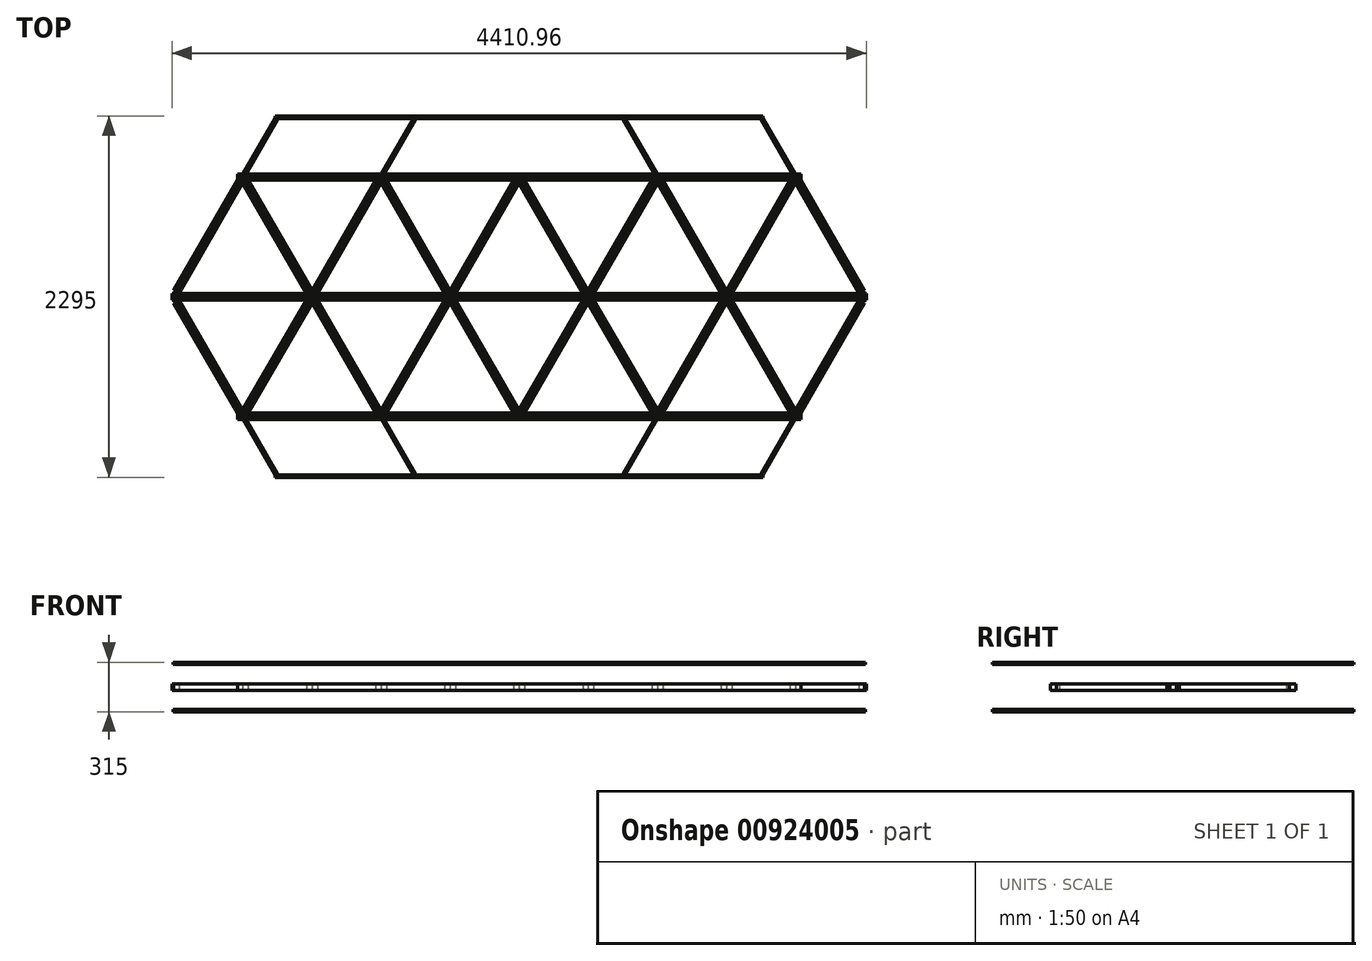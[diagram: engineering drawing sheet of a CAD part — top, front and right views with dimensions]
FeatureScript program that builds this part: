
annotation { "Feature Type Name" : "Feature", "Feature Type Description" : "" }
export const myFeature = defineFeature(function(context is Context, id is Id, definition is map)
    precondition{}
    {
        {
            var Q0;
            Q0=qCreatedBy(makeId("Top.planeOp"),FACE);
            var sketch = newSketch(context, id + "F0", { "sketchPlane" : qUnion([Q0])});
            skLineSegment(sketch, "E0", {"start": v(-2194.22, 0) * mm, "end": v(2196.22, 0) * mm, "construction": true});
            skLineSegment(sketch, "E1", {"start": v(0, 0.48) * mm, "end": v(0, -0.7) * mm, "construction": true});
            skLineSegment(sketch, "E2", {"start": v(0, 760) * mm, "end": v(438.79, 0) * mm, "construction": true});
            skLineSegment(sketch, "E3", {"start": v(438.79, 0) * mm, "end": v(877.57, 760) * mm, "construction": true});
            skLineSegment(sketch, "E4", {"start": v(0, 760) * mm, "end": v(877.57, 760) * mm, "construction": true});
            skLineSegment(sketch, "E5", {"start": v(877.57, 760) * mm, "end": v(877.57, 744.9) * mm, "construction": true});
            skLineSegment(sketch, "E6.MirrorCS", {"start": v(1316.36, 0) * mm, "end": v(877.57, 760) * mm, "construction": true});
            skLineSegment(sketch, "E7.MirrorCS", {"start": v(1755.14, 760) * mm, "end": v(1316.36, 0) * mm, "construction": true});
            skLineSegment(sketch, "E8.MirrorCS", {"start": v(1755.14, 760) * mm, "end": v(877.57, 760) * mm, "construction": true});
            skLineSegment(sketch, "E9", {"start": v(1755.14, 760) * mm, "end": v(1755.14, 750.7) * mm, "construction": true});
            skLineSegment(sketch, "E10.MirrorCS", {"start": v(1755.14, 760) * mm, "end": v(2193.93, 0) * mm, "construction": true});
            skLineSegment(sketch, "E11.MirrorCS", {"start": v(0, -760) * mm, "end": v(438.79, 0) * mm, "construction": true});
            skLineSegment(sketch, "E12.MirrorCS", {"start": v(438.79, 0) * mm, "end": v(877.57, -760) * mm, "construction": true});
            skLineSegment(sketch, "E13.MirrorCS", {"start": v(1316.36, 0) * mm, "end": v(877.57, -760) * mm, "construction": true});
            skLineSegment(sketch, "E14.MirrorCS", {"start": v(1755.14, -760) * mm, "end": v(1316.36, 0) * mm, "construction": true});
            skLineSegment(sketch, "E15.MirrorCS", {"start": v(1755.14, -760) * mm, "end": v(2193.93, 0) * mm, "construction": true});
            skLineSegment(sketch, "E16.MirrorCS", {"start": v(1755.14, -760) * mm, "end": v(877.57, -760) * mm, "construction": true});
            skLineSegment(sketch, "E17.MirrorCS", {"start": v(0, -760) * mm, "end": v(877.57, -760) * mm, "construction": true});
            skLineSegment(sketch, "E18.MirrorCS", {"start": v(-438.79, 0) * mm, "end": v(-877.57, -760) * mm, "construction": true});
            skLineSegment(sketch, "E19.MirrorCS", {"start": v(0, 760) * mm, "end": v(-438.79, 0) * mm, "construction": true});
            skLineSegment(sketch, "E20.MirrorCS", {"start": v(-438.79, 0) * mm, "end": v(-877.57, 760) * mm, "construction": true});
            skLineSegment(sketch, "E21.MirrorCS", {"start": v(0, 760) * mm, "end": v(-877.57, 760) * mm, "construction": true});
            skLineSegment(sketch, "E22.MirrorCS", {"start": v(-877.57, 760) * mm, "end": v(-877.57, 744.9) * mm, "construction": true});
            skLineSegment(sketch, "E23.MirrorCS", {"start": v(0, -760) * mm, "end": v(-438.79, 0) * mm, "construction": true});
            skLineSegment(sketch, "E24.MirrorCS", {"start": v(-1755.14, 760) * mm, "end": v(-1755.14, 750.7) * mm, "construction": true});
            skLineSegment(sketch, "E25.MirrorCS", {"start": v(-1316.36, 0) * mm, "end": v(-877.57, 760) * mm, "construction": true});
            skLineSegment(sketch, "E26.MirrorCS", {"start": v(-1755.14, 760) * mm, "end": v(-877.57, 760) * mm, "construction": true});
            skLineSegment(sketch, "E27.MirrorCS", {"start": v(-1755.14, -760) * mm, "end": v(-877.57, -760) * mm, "construction": true});
            skLineSegment(sketch, "E28.MirrorCS", {"start": v(-1755.14, 760) * mm, "end": v(-1316.36, 0) * mm, "construction": true});
            skLineSegment(sketch, "E29.MirrorCS", {"start": v(-1755.14, -760) * mm, "end": v(-2193.93, 0) * mm, "construction": true});
            skLineSegment(sketch, "E30.MirrorCS", {"start": v(-1316.36, 0) * mm, "end": v(-877.57, -760) * mm, "construction": true});
            skLineSegment(sketch, "E31.MirrorCS", {"start": v(-1755.14, -760) * mm, "end": v(-1316.36, 0) * mm, "construction": true});
            skLineSegment(sketch, "E32.MirrorCS", {"start": v(-1755.14, 760) * mm, "end": v(-2193.93, 0) * mm, "construction": true});
            skLineSegment(sketch, "E33.MirrorCS", {"start": v(0, -760) * mm, "end": v(-877.57, -760) * mm, "construction": true});
            skCircle(sketch, "E34", {"center": v(438.79, 760) * mm, "radius": 380 * mm, "construction": true});
            skLineSegment(sketch, "E35", {"start": v(438.79, 0) * mm, "end": v(1316.36, 0) * mm, "construction": true});
            skCircle(sketch, "E36", {"center": v(877.57, 0) * mm, "radius": 380 * mm, "construction": true});
            skLineSegment(sketch, "E37", {"start": v(1316.36, 0) * mm, "end": v(1316.36, -2.45) * mm, "construction": true});
            skCircle(sketch, "E38.MirrorC", {"center": v(1755.14, 0) * mm, "radius": 380 * mm, "construction": true});
            skCircle(sketch, "E39.MirrorC", {"center": v(1316.36, 760) * mm, "radius": 380 * mm, "construction": true});
            skCircle(sketch, "E40.MirrorC", {"center": v(1316.36, -760) * mm, "radius": 380 * mm, "construction": true});
            skCircle(sketch, "E41.MirrorC", {"center": v(438.79, -760) * mm, "radius": 380 * mm, "construction": true});
            skCircle(sketch, "E42.MirrorC", {"center": v(-438.79, 760) * mm, "radius": 380 * mm, "construction": true});
            skCircle(sketch, "E43.MirrorC", {"center": v(-1316.36, 760) * mm, "radius": 380 * mm, "construction": true});
            skCircle(sketch, "E44.MirrorC", {"center": v(-877.57, 0) * mm, "radius": 380 * mm, "construction": true});
            skCircle(sketch, "E45.MirrorC", {"center": v(-1755.14, 0) * mm, "radius": 380 * mm, "construction": true});
            skCircle(sketch, "E46.MirrorC", {"center": v(-1316.36, -760) * mm, "radius": 380 * mm, "construction": true});
            skCircle(sketch, "E47.MirrorC", {"center": v(-438.79, -760) * mm, "radius": 380 * mm, "construction": true});
            skLineSegment(sketch, "E48", {"start": v(0, 1140) * mm, "end": v(1535.75, 1140) * mm, "construction": true});
            skLineSegment(sketch, "E49", {"start": v(1535.75, 1140) * mm, "end": v(1755.14, 760) * mm, "construction": true});
            skLineSegment(sketch, "E50.MirrorCS", {"start": v(0, -1140) * mm, "end": v(1535.75, -1140) * mm, "construction": true});
            skLineSegment(sketch, "E51.MirrorCS", {"start": v(1535.75, -1140) * mm, "end": v(1755.14, -760) * mm, "construction": true});
            skLineSegment(sketch, "E52.MirrorCS", {"start": v(0, 1140) * mm, "end": v(-1535.75, 1140) * mm, "construction": true});
            skLineSegment(sketch, "E53.MirrorCS", {"start": v(-1535.75, 1140) * mm, "end": v(-1755.14, 760) * mm, "construction": true});
            skLineSegment(sketch, "E54.MirrorCS", {"start": v(-1535.75, -1140) * mm, "end": v(-1755.14, -760) * mm, "construction": true});
            skLineSegment(sketch, "E55.MirrorCS", {"start": v(0, -1140) * mm, "end": v(-1535.75, -1140) * mm, "construction": true});
            skSolve(sketch);
        }
        {
            var Q0;
            Q0=qCreatedBy(makeId("Top.planeOp"),FACE);
            var sketch = newSketch(context, id + "F1", { "sketchPlane" : qUnion([Q0])});
            skCircle(sketch, "E56.0", {"center": v(1316.36, 760) * mm, "radius": 380 * mm, "construction": true});
            skCircle(sketch, "E57.0", {"center": v(438.79, 760) * mm, "radius": 380 * mm, "construction": true});
            skCircle(sketch, "E58.0", {"center": v(877.57, 0) * mm, "radius": 380 * mm, "construction": true});
            skCircle(sketch, "E59.0", {"center": v(1755.14, 0) * mm, "radius": 380 * mm, "construction": true});
            skCircle(sketch, "E60.0", {"center": v(1316.36, -760) * mm, "radius": 380 * mm, "construction": true});
            skCircle(sketch, "E61.0", {"center": v(438.79, -760) * mm, "radius": 380 * mm, "construction": true});
            skCircle(sketch, "E62.0", {"center": v(-438.79, -760) * mm, "radius": 380 * mm, "construction": true});
            skCircle(sketch, "E63.0", {"center": v(-877.57, 0) * mm, "radius": 380 * mm, "construction": true});
            skCircle(sketch, "E64.0", {"center": v(-1316.36, -760) * mm, "radius": 380 * mm, "construction": true});
            skCircle(sketch, "E65.0", {"center": v(-1755.14, 0) * mm, "radius": 380 * mm, "construction": true});
            skCircle(sketch, "E66.0", {"center": v(-1316.36, 760) * mm, "radius": 380 * mm, "construction": true});
            skCircle(sketch, "E67.0", {"center": v(-438.79, 760) * mm, "radius": 380 * mm, "construction": true});
            skLineSegment(sketch, "E68.0", {"start": v(0, 1140) * mm, "end": v(1535.75, 1140) * mm, "construction": true});
            skLineSegment(sketch, "E69.0", {"start": v(1535.75, 1140) * mm, "end": v(1755.14, 760) * mm, "construction": true});
            skLineSegment(sketch, "E70.0", {"start": v(1755.14, 760) * mm, "end": v(2193.93, 0) * mm, "construction": true});
            skLineSegment(sketch, "E71.0", {"start": v(1755.14, -760) * mm, "end": v(2193.93, 0) * mm, "construction": true});
            skLineSegment(sketch, "E72.0", {"start": v(1535.75, -1140) * mm, "end": v(1755.14, -760) * mm, "construction": true});
            skLineSegment(sketch, "E73.0", {"start": v(0, -1140) * mm, "end": v(1535.75, -1140) * mm, "construction": true});
            skLineSegment(sketch, "E74.0", {"start": v(0, -1140) * mm, "end": v(-1535.75, -1140) * mm, "construction": true});
            skLineSegment(sketch, "E75.0", {"start": v(-1535.75, -1140) * mm, "end": v(-1755.14, -760) * mm, "construction": true});
            skLineSegment(sketch, "E76.0", {"start": v(-1755.14, -760) * mm, "end": v(-2193.93, 0) * mm, "construction": true});
            skLineSegment(sketch, "E77.0", {"start": v(-1755.14, 760) * mm, "end": v(-2193.93, 0) * mm, "construction": true});
            skLineSegment(sketch, "E78.0", {"start": v(-1535.75, 1140) * mm, "end": v(-1755.14, 760) * mm, "construction": true});
            skLineSegment(sketch, "E79.0", {"start": v(0, 1140) * mm, "end": v(-1535.75, 1140) * mm, "construction": true});
            skLineSegment(sketch, "E80.0", {"start": v(0, 2.22) * mm, "end": v(0, -2.6) * mm, "construction": true});
            skLineSegment(sketch, "E80.1", {"start": v(-2198.4, 0) * mm, "end": v(2196.46, 0) * mm, "construction": true});
            skLineSegment(sketch, "E81", {"start": v(0, 0) * mm, "end": v(438.79, 760) * mm, "construction": true});
            skLineSegment(sketch, "E82", {"start": v(438.79, 760) * mm, "end": v(438.79, 720.57) * mm, "construction": true});
            skLineSegment(sketch, "E83.MirrorCS", {"start": v(877.57, 0) * mm, "end": v(438.79, 760) * mm, "construction": true});
            skLineSegment(sketch, "E84", {"start": v(877.57, 0) * mm, "end": v(877.57, 11.38) * mm, "construction": true});
            skLineSegment(sketch, "E85.MirrorCS", {"start": v(877.57, 0) * mm, "end": v(1316.36, 760) * mm, "construction": true});
            skLineSegment(sketch, "E86.MirrorCS", {"start": v(877.57, 0) * mm, "end": v(1316.36, -760) * mm, "construction": true});
            skLineSegment(sketch, "E87.MirrorCS", {"start": v(877.57, 0) * mm, "end": v(438.79, -760) * mm, "construction": true});
            skLineSegment(sketch, "E88.MirrorCS", {"start": v(0, 0) * mm, "end": v(438.79, -760) * mm, "construction": true});
            skLineSegment(sketch, "E89.MirrorCS", {"start": v(0, 0) * mm, "end": v(-438.79, 760) * mm, "construction": true});
            skLineSegment(sketch, "E90.MirrorCS", {"start": v(0, 0) * mm, "end": v(-438.79, -760) * mm, "construction": true});
            skLineSegment(sketch, "E91.MirrorCS", {"start": v(-877.57, 0) * mm, "end": v(-438.79, 760) * mm, "construction": true});
            skLineSegment(sketch, "E92.MirrorCS", {"start": v(-877.57, 0) * mm, "end": v(-438.79, -760) * mm, "construction": true});
            skLineSegment(sketch, "E93.MirrorCS", {"start": v(-877.57, 0) * mm, "end": v(-1316.36, 760) * mm, "construction": true});
            skLineSegment(sketch, "E94.MirrorCS", {"start": v(-877.57, 0) * mm, "end": v(-1316.36, -760) * mm, "construction": true});
            skLineSegment(sketch, "E95", {"start": v(438.79, 760) * mm, "end": v(438.79, 1140) * mm, "construction": true});
            skLineSegment(sketch, "E96", {"start": v(1316.36, 760) * mm, "end": v(1535.75, 1140) * mm, "construction": true});
            skLineSegment(sketch, "E97.MirrorCS", {"start": v(438.79, -760) * mm, "end": v(438.79, -1140) * mm, "construction": true});
            skLineSegment(sketch, "E98.MirrorCS", {"start": v(1316.36, -760) * mm, "end": v(1535.75, -1140) * mm, "construction": true});
            skLineSegment(sketch, "E99.MirrorCS", {"start": v(-438.79, 760) * mm, "end": v(-438.79, 1140) * mm, "construction": true});
            skLineSegment(sketch, "E100.MirrorCS", {"start": v(-1316.36, 760) * mm, "end": v(-1535.75, 1140) * mm, "construction": true});
            skLineSegment(sketch, "E101.MirrorCS", {"start": v(-1316.36, -760) * mm, "end": v(-1535.75, -1140) * mm, "construction": true});
            skLineSegment(sketch, "E102.MirrorCS", {"start": v(-438.79, -760) * mm, "end": v(-438.79, -1140) * mm, "construction": true});
            skSolve(sketch);
        }
        {
            var Q0;
            Q0=qCreatedBy(makeId("Top.planeOp"),FACE);
            var sketch = newSketch(context, id + "F2", { "sketchPlane" : qUnion([Q0])});
            skLineSegment(sketch, "E103", {"start": v(-2205.48, 20) * mm, "end": v(0, 20) * mm});
            skLineSegment(sketch, "E104", {"start": v(-2205.48, -20) * mm, "end": v(0, -20) * mm});
            skLineSegment(sketch, "E105", {"start": v(0, 20) * mm, "end": v(0, 798.26) * mm, "construction": true});
            skLineSegment(sketch, "E106", {"start": v(-1789.79, 780) * mm, "end": v(0, 780) * mm});
            skLineSegment(sketch, "E107", {"start": v(-1789.79, 740) * mm, "end": v(0, 740) * mm});
            skLineSegment(sketch, "E108", {"start": v(-1789.79, 780) * mm, "end": v(-1789.79, 740) * mm});
            skLineSegment(sketch, "E109", {"start": v(-1737.82, 730) * mm, "end": v(-1720.5, 740) * mm});
            skLineSegment(sketch, "E110", {"start": v(-1720.5, 740) * mm, "end": v(-1316.36, 40) * mm});
            skLineSegment(sketch, "E111", {"start": v(-1316.36, 40) * mm, "end": v(-1333.68, 30) * mm});
            skLineSegment(sketch, "E112.MirrorCS", {"start": v(-1737.82, 730) * mm, "end": v(-1755.14, 720) * mm});
            skLineSegment(sketch, "E113.MirrorCS", {"start": v(-1755.14, 720) * mm, "end": v(-1351, 20) * mm});
            skLineSegment(sketch, "E114.MirrorCS", {"start": v(-1351, 20) * mm, "end": v(-1333.68, 30) * mm});
            skLineSegment(sketch, "E115", {"start": v(-1316.36, 0) * mm, "end": v(-1316.36, 20) * mm, "construction": true});
            skLineSegment(sketch, "E116.MirrorCS", {"start": v(-912.21, 740) * mm, "end": v(-1316.36, 40) * mm});
            skLineSegment(sketch, "E117.MirrorCS", {"start": v(-1316.36, 40) * mm, "end": v(-1299.04, 30) * mm});
            skLineSegment(sketch, "E118.MirrorCS", {"start": v(-1281.72, 20) * mm, "end": v(-1299.04, 30) * mm});
            skLineSegment(sketch, "E119.MirrorCS", {"start": v(-877.57, 720) * mm, "end": v(-1281.72, 20) * mm});
            skLineSegment(sketch, "E120.MirrorCS", {"start": v(-894.9, 730) * mm, "end": v(-912.21, 740) * mm});
            skLineSegment(sketch, "E121.MirrorCS", {"start": v(-894.9, 730) * mm, "end": v(-877.57, 720) * mm});
            skLineSegment(sketch, "E122.MirrorCS", {"start": v(-860.25, 730) * mm, "end": v(-877.57, 720) * mm});
            skLineSegment(sketch, "E123.MirrorCS", {"start": v(-860.25, 730) * mm, "end": v(-842.93, 740) * mm});
            skLineSegment(sketch, "E124.MirrorCS", {"start": v(-842.93, 740) * mm, "end": v(-438.79, 40) * mm});
            skLineSegment(sketch, "E125.MirrorCS", {"start": v(-877.57, 720) * mm, "end": v(-473.43, 20) * mm});
            skLineSegment(sketch, "E126.MirrorCS", {"start": v(-438.79, 40) * mm, "end": v(-456.1, 30) * mm});
            skLineSegment(sketch, "E127.MirrorCS", {"start": v(-473.43, 20) * mm, "end": v(-456.1, 30) * mm});
            skLineSegment(sketch, "E128", {"start": v(-438.79, 0) * mm, "end": v(-438.79, 20) * mm, "construction": true});
            skLineSegment(sketch, "E129.MirrorCS", {"start": v(-34.64, 740) * mm, "end": v(-438.79, 40) * mm});
            skLineSegment(sketch, "E130.MirrorCS", {"start": v(-438.79, 40) * mm, "end": v(-421.47, 30) * mm});
            skLineSegment(sketch, "E131.MirrorCS", {"start": v(-404.15, 20) * mm, "end": v(-421.47, 30) * mm});
            skLineSegment(sketch, "E132.MirrorCS", {"start": v(0, 720) * mm, "end": v(-404.15, 20) * mm});
            skLineSegment(sketch, "E133.MirrorCS", {"start": v(-17.32, 730) * mm, "end": v(0, 720) * mm});
            skLineSegment(sketch, "E134.MirrorCS", {"start": v(-17.32, 730) * mm, "end": v(-34.64, 740) * mm});
            skLineSegment(sketch, "E135.MirrorCS", {"start": v(1789.79, 740) * mm, "end": v(0, 740) * mm});
            skLineSegment(sketch, "E136.MirrorCS", {"start": v(1789.79, 780) * mm, "end": v(0, 780) * mm});
            skLineSegment(sketch, "E137.MirrorCS", {"start": v(1789.79, 780) * mm, "end": v(1789.79, 740) * mm});
            skLineSegment(sketch, "E138.MirrorCS", {"start": v(17.32, 730) * mm, "end": v(34.64, 740) * mm});
            skLineSegment(sketch, "E139.MirrorCS", {"start": v(17.32, 730) * mm, "end": v(0, 720) * mm});
            skLineSegment(sketch, "E140.MirrorCS", {"start": v(34.64, 740) * mm, "end": v(438.79, 40) * mm});
            skLineSegment(sketch, "E141.MirrorCS", {"start": v(0, 720) * mm, "end": v(404.15, 20) * mm});
            skLineSegment(sketch, "E142.MirrorCS", {"start": v(438.79, 40) * mm, "end": v(421.47, 30) * mm});
            skLineSegment(sketch, "E143.MirrorCS", {"start": v(404.15, 20) * mm, "end": v(421.47, 30) * mm});
            skLineSegment(sketch, "E144.MirrorCS", {"start": v(438.79, 40) * mm, "end": v(456.1, 30) * mm});
            skLineSegment(sketch, "E145.MirrorCS", {"start": v(473.43, 20) * mm, "end": v(456.1, 30) * mm});
            skLineSegment(sketch, "E146.MirrorCS", {"start": v(877.57, 720) * mm, "end": v(473.43, 20) * mm});
            skLineSegment(sketch, "E147.MirrorCS", {"start": v(842.93, 740) * mm, "end": v(438.79, 40) * mm});
            skLineSegment(sketch, "E148.MirrorCS", {"start": v(860.25, 730) * mm, "end": v(877.57, 720) * mm});
            skLineSegment(sketch, "E149.MirrorCS", {"start": v(860.25, 730) * mm, "end": v(842.93, 740) * mm});
            skLineSegment(sketch, "E150.MirrorCS", {"start": v(894.9, 730) * mm, "end": v(877.57, 720) * mm});
            skLineSegment(sketch, "E151.MirrorCS", {"start": v(894.9, 730) * mm, "end": v(912.21, 740) * mm});
            skLineSegment(sketch, "E152.MirrorCS", {"start": v(912.21, 740) * mm, "end": v(1316.36, 40) * mm});
            skLineSegment(sketch, "E153.MirrorCS", {"start": v(877.57, 720) * mm, "end": v(1281.72, 20) * mm});
            skLineSegment(sketch, "E154.MirrorCS", {"start": v(1316.36, 40) * mm, "end": v(1299.04, 30) * mm});
            skLineSegment(sketch, "E155.MirrorCS", {"start": v(1281.72, 20) * mm, "end": v(1299.04, 30) * mm});
            skLineSegment(sketch, "E156.MirrorCS", {"start": v(1316.36, 40) * mm, "end": v(1333.68, 30) * mm});
            skLineSegment(sketch, "E157.MirrorCS", {"start": v(1351, 20) * mm, "end": v(1333.68, 30) * mm});
            skLineSegment(sketch, "E158.MirrorCS", {"start": v(1755.14, 720) * mm, "end": v(1351, 20) * mm});
            skLineSegment(sketch, "E159.MirrorCS", {"start": v(1720.5, 740) * mm, "end": v(1316.36, 40) * mm});
            skLineSegment(sketch, "E160.MirrorCS", {"start": v(1737.82, 730) * mm, "end": v(1755.14, 720) * mm});
            skLineSegment(sketch, "E161.MirrorCS", {"start": v(1737.82, 730) * mm, "end": v(1720.5, 740) * mm});
            skLineSegment(sketch, "E162.MirrorCS", {"start": v(-1772.47, 730) * mm, "end": v(-1755.14, 720) * mm});
            skLineSegment(sketch, "E163.MirrorCS", {"start": v(-1772.47, 730) * mm, "end": v(-1789.79, 740) * mm});
            skLineSegment(sketch, "E164.MirrorCS", {"start": v(1772.47, 730) * mm, "end": v(1755.14, 720) * mm});
            skLineSegment(sketch, "E165.MirrorCS", {"start": v(1772.47, 730) * mm, "end": v(1789.79, 740) * mm});
            skLineSegment(sketch, "E166", {"start": v(-1789.79, 740) * mm, "end": v(-2193.93, 40) * mm});
            skLineSegment(sketch, "E167", {"start": v(-2205.48, 20) * mm, "end": v(-2205.48, -20) * mm});
            skLineSegment(sketch, "E168", {"start": v(-2193.93, 40) * mm, "end": v(-2159.3, 20) * mm});
            skLineSegment(sketch, "E169", {"start": v(-2159.3, 20) * mm, "end": v(-1755.14, 720) * mm});
            skLineSegment(sketch, "E170", {"start": v(-2193.93, 40) * mm, "end": v(-2205.48, 20) * mm, "construction": true});
            skPoint(sketch, "E171", {"position": v(-877.57, 760) * mm});
            skLineSegment(sketch, "E172.MirrorCS", {"start": v(-1351, -20) * mm, "end": v(-1333.68, -30) * mm});
            skLineSegment(sketch, "E173.MirrorCS", {"start": v(-438.79, -40) * mm, "end": v(-421.47, -30) * mm});
            skLineSegment(sketch, "E174.MirrorCS", {"start": v(-1316.36, -40) * mm, "end": v(-1299.04, -30) * mm});
            skLineSegment(sketch, "E175.MirrorCS", {"start": v(-438.79, -40) * mm, "end": v(-456.1, -30) * mm});
            skLineSegment(sketch, "E176.MirrorCS", {"start": v(-1316.36, -40) * mm, "end": v(-1333.68, -30) * mm});
            skLineSegment(sketch, "E177.MirrorCS", {"start": v(-860.25, -730) * mm, "end": v(-842.93, -740) * mm});
            skLineSegment(sketch, "E178.MirrorCS", {"start": v(17.32, -730) * mm, "end": v(0, -720) * mm});
            skLineSegment(sketch, "E179.MirrorCS", {"start": v(-1737.82, -730) * mm, "end": v(-1755.14, -720) * mm});
            skLineSegment(sketch, "E180.MirrorCS", {"start": v(-860.25, -730) * mm, "end": v(-877.57, -720) * mm});
            skLineSegment(sketch, "E181.MirrorCS", {"start": v(860.25, -730) * mm, "end": v(877.57, -720) * mm});
            skLineSegment(sketch, "E182.MirrorCS", {"start": v(438.79, -40) * mm, "end": v(421.47, -30) * mm});
            skLineSegment(sketch, "E183.MirrorCS", {"start": v(-1772.47, -730) * mm, "end": v(-1755.14, -720) * mm});
            skLineSegment(sketch, "E184.MirrorCS", {"start": v(1281.72, -20) * mm, "end": v(1299.04, -30) * mm});
            skLineSegment(sketch, "E185.MirrorCS", {"start": v(438.79, -40) * mm, "end": v(456.1, -30) * mm});
            skLineSegment(sketch, "E186.MirrorCS", {"start": v(894.9, -730) * mm, "end": v(877.57, -720) * mm});
            skLineSegment(sketch, "E187.MirrorCS", {"start": v(-1772.47, -730) * mm, "end": v(-1789.79, -740) * mm});
            skLineSegment(sketch, "E188.MirrorCS", {"start": v(1316.36, -40) * mm, "end": v(1333.68, -30) * mm});
            skLineSegment(sketch, "E189.MirrorCS", {"start": v(-894.9, -730) * mm, "end": v(-877.57, -720) * mm});
            skLineSegment(sketch, "E190.MirrorCS", {"start": v(-17.32, -730) * mm, "end": v(-34.64, -740) * mm});
            skLineSegment(sketch, "E191.MirrorCS", {"start": v(473.43, -20) * mm, "end": v(456.1, -30) * mm});
            skLineSegment(sketch, "E192.MirrorCS", {"start": v(1772.47, -730) * mm, "end": v(1789.79, -740) * mm});
            skLineSegment(sketch, "E193.MirrorCS", {"start": v(-17.32, -730) * mm, "end": v(0, -720) * mm});
            skLineSegment(sketch, "E194.MirrorCS", {"start": v(1316.36, -40) * mm, "end": v(1299.04, -30) * mm});
            skLineSegment(sketch, "E195.MirrorCS", {"start": v(-2193.93, -40) * mm, "end": v(-2205.48, -20) * mm, "construction": true});
            skLineSegment(sketch, "E196.MirrorCS", {"start": v(1737.82, -730) * mm, "end": v(1755.14, -720) * mm});
            skLineSegment(sketch, "E197.MirrorCS", {"start": v(1772.47, -730) * mm, "end": v(1755.14, -720) * mm});
            skLineSegment(sketch, "E198.MirrorCS", {"start": v(-2193.93, -40) * mm, "end": v(-2159.3, -20) * mm});
            skLineSegment(sketch, "E199.MirrorCS", {"start": v(-894.9, -730) * mm, "end": v(-912.21, -740) * mm});
            skLineSegment(sketch, "E200.MirrorCS", {"start": v(404.15, -20) * mm, "end": v(421.47, -30) * mm});
            skLineSegment(sketch, "E201.MirrorCS", {"start": v(-404.15, -20) * mm, "end": v(-421.47, -30) * mm});
            skLineSegment(sketch, "E202.MirrorCS", {"start": v(1789.79, -780) * mm, "end": v(1789.79, -740) * mm});
            skLineSegment(sketch, "E203.MirrorCS", {"start": v(-1281.72, -20) * mm, "end": v(-1299.04, -30) * mm});
            skLineSegment(sketch, "E204.MirrorCS", {"start": v(1737.82, -730) * mm, "end": v(1720.5, -740) * mm});
            skLineSegment(sketch, "E205.MirrorCS", {"start": v(860.25, -730) * mm, "end": v(842.93, -740) * mm});
            skLineSegment(sketch, "E206.MirrorCS", {"start": v(-1737.82, -730) * mm, "end": v(-1720.5, -740) * mm});
            skLineSegment(sketch, "E207.MirrorCS", {"start": v(1351, -20) * mm, "end": v(1333.68, -30) * mm});
            skLineSegment(sketch, "E208.MirrorCS", {"start": v(894.9, -730) * mm, "end": v(912.21, -740) * mm});
            skLineSegment(sketch, "E209.MirrorCS", {"start": v(-473.43, -20) * mm, "end": v(-456.1, -30) * mm});
            skLineSegment(sketch, "E210.MirrorCS", {"start": v(-1789.79, -780) * mm, "end": v(-1789.79, -740) * mm});
            skLineSegment(sketch, "E211.MirrorCS", {"start": v(17.32, -730) * mm, "end": v(34.64, -740) * mm});
            skLineSegment(sketch, "E212.MirrorCS", {"start": v(-1755.14, -720) * mm, "end": v(-1351, -20) * mm});
            skLineSegment(sketch, "E213.MirrorCS", {"start": v(-1789.79, -780) * mm, "end": v(0, -780) * mm});
            skLineSegment(sketch, "E214.MirrorCS", {"start": v(-842.93, -740) * mm, "end": v(-438.79, -40) * mm});
            skLineSegment(sketch, "E215.MirrorCS", {"start": v(-877.57, -720) * mm, "end": v(-473.43, -20) * mm});
            skLineSegment(sketch, "E216.MirrorCS", {"start": v(842.93, -740) * mm, "end": v(438.79, -40) * mm});
            skLineSegment(sketch, "E217.MirrorCS", {"start": v(34.64, -740) * mm, "end": v(438.79, -40) * mm});
            skLineSegment(sketch, "E218.MirrorCS", {"start": v(1755.14, -720) * mm, "end": v(1351, -20) * mm});
            skLineSegment(sketch, "E219.MirrorCS", {"start": v(-1720.5, -740) * mm, "end": v(-1316.36, -40) * mm});
            skLineSegment(sketch, "E220.MirrorCS", {"start": v(-1789.79, -740) * mm, "end": v(-2193.93, -40) * mm});
            skLineSegment(sketch, "E221.MirrorCS", {"start": v(0, -720) * mm, "end": v(-404.15, -20) * mm});
            skLineSegment(sketch, "E222.MirrorCS", {"start": v(-2159.3, -20) * mm, "end": v(-1755.14, -720) * mm});
            skLineSegment(sketch, "E223.MirrorCS", {"start": v(1720.5, -740) * mm, "end": v(1316.36, -40) * mm});
            skLineSegment(sketch, "E224.MirrorCS", {"start": v(877.57, -720) * mm, "end": v(1281.72, -20) * mm});
            skLineSegment(sketch, "E225.MirrorCS", {"start": v(877.57, -720) * mm, "end": v(473.43, -20) * mm});
            skLineSegment(sketch, "E226.MirrorCS", {"start": v(-912.21, -740) * mm, "end": v(-1316.36, -40) * mm});
            skLineSegment(sketch, "E227.MirrorCS", {"start": v(-34.64, -740) * mm, "end": v(-438.79, -40) * mm});
            skLineSegment(sketch, "E228.MirrorCS", {"start": v(1789.79, -740) * mm, "end": v(0, -740) * mm});
            skLineSegment(sketch, "E229.MirrorCS", {"start": v(912.21, -740) * mm, "end": v(1316.36, -40) * mm});
            skPoint(sketch, "E230.MirrorP", {"position": v(-877.57, -760) * mm});
            skLineSegment(sketch, "E231.MirrorCS", {"start": v(-877.57, -720) * mm, "end": v(-1281.72, -20) * mm});
            skLineSegment(sketch, "E232.MirrorCS", {"start": v(0, -720) * mm, "end": v(404.15, -20) * mm});
            skLineSegment(sketch, "E233.MirrorCS", {"start": v(-1789.79, -740) * mm, "end": v(0, -740) * mm});
            skLineSegment(sketch, "E234.MirrorCS", {"start": v(2205.48, 20) * mm, "end": v(0, 20) * mm});
            skLineSegment(sketch, "E235.MirrorCS", {"start": v(2205.48, -20) * mm, "end": v(0, -20) * mm});
            skLineSegment(sketch, "E236.MirrorCS", {"start": v(2205.48, 20) * mm, "end": v(2205.48, -20) * mm});
            skLineSegment(sketch, "E237.MirrorCS", {"start": v(2159.3, 20) * mm, "end": v(1755.14, 720) * mm});
            skLineSegment(sketch, "E238.MirrorCS", {"start": v(2193.93, 40) * mm, "end": v(2159.3, 20) * mm});
            skLineSegment(sketch, "E239.MirrorCS", {"start": v(1789.79, 740) * mm, "end": v(2193.93, 40) * mm});
            skLineSegment(sketch, "E240.MirrorCS", {"start": v(2159.3, -20) * mm, "end": v(1755.14, -720) * mm});
            skLineSegment(sketch, "E241.MirrorCS", {"start": v(2193.93, -40) * mm, "end": v(2159.3, -20) * mm});
            skLineSegment(sketch, "E242.MirrorCS", {"start": v(1789.79, -740) * mm, "end": v(2193.93, -40) * mm});
            skLineSegment(sketch, "E243.MirrorCS", {"start": v(1789.79, -780) * mm, "end": v(0, -780) * mm});
            skSolve(sketch);
        }
        {
            var Q0;
            Q0=qCreatedBy(makeId("Top.planeOp"),FACE);
            cPlane(context, id + "F3", {"entities" : qUnion([Q0]), "cplaneType" : CPlaneType.OFFSET, "offset" : 150 * mm, "width" : 150 * mm, "height" : 150 * mm});
        }
        {
            var Q0;
            {var subQ0=sQuery(id+"F2.wireOp",EDGE,"E108");Q0=makeQuery(id+"F2.imprint","IMPRINT",FACE,{"disambiguationData":[TD([[makeQuery(id+"F2.imprint","IMPRINT",EDGE,{"derivedFrom":subQ0}),1.0]])]});}
            var Q1;
            Q1=makeQuery(id+"F2.imprint","IMPRINT",FACE,{"disambiguationData":[TD([[makeQuery(id+"F2.imprint","IMPRINT",EDGE,{"derivedFrom":sQuery(id+"F2.wireOp",EDGE,"E162.MirrorCS")}),-1.0]])]});
            var Q2;
            Q2=makeQuery(id+"F2.imprint","IMPRINT",FACE,{"disambiguationData":[TD([[makeQuery(id+"F2.imprint","IMPRINT",EDGE,{"derivedFrom":sQuery(id+"F2.wireOp",EDGE,"E109")}),-1.0]])]});
            var Q3;
            Q3=makeQuery(id+"F2.imprint","IMPRINT",FACE,{"disambiguationData":[TD([[makeQuery(id+"F2.imprint","IMPRINT",EDGE,{"derivedFrom":sQuery(id+"F2.wireOp",EDGE,"E116.MirrorCS")}),1.0]])]});
            var Q4;
            Q4=makeQuery(id+"F2.imprint","IMPRINT",FACE,{"disambiguationData":[TD([[makeQuery(id+"F2.imprint","IMPRINT",EDGE,{"derivedFrom":sQuery(id+"F2.wireOp",EDGE,"E122.MirrorCS")}),1.0]])]});
            var Q5;
            Q5=makeQuery(id+"F2.imprint","IMPRINT",FACE,{"disambiguationData":[TD([[makeQuery(id+"F2.imprint","IMPRINT",EDGE,{"derivedFrom":sQuery(id+"F2.wireOp",EDGE,"E129.MirrorCS")}),1.0]])]});
            var Q6;
            Q6=makeQuery(id+"F2.imprint","IMPRINT",FACE,{"disambiguationData":[TD([[makeQuery(id+"F2.imprint","IMPRINT",EDGE,{"derivedFrom":sQuery(id+"F2.wireOp",EDGE,"E138.MirrorCS")}),-1.0]])]});
            var Q7;
            Q7=makeQuery(id+"F2.imprint","IMPRINT",FACE,{"disambiguationData":[TD([[makeQuery(id+"F2.imprint","IMPRINT",EDGE,{"derivedFrom":sQuery(id+"F2.wireOp",EDGE,"E144.MirrorCS")}),1.0]])]});
            var Q8;
            Q8=makeQuery(id+"F2.imprint","IMPRINT",FACE,{"disambiguationData":[TD([[makeQuery(id+"F2.imprint","IMPRINT",EDGE,{"derivedFrom":sQuery(id+"F2.wireOp",EDGE,"E150.MirrorCS")}),1.0]])]});
            var Q9;
            Q9=makeQuery(id+"F2.imprint","IMPRINT",FACE,{"disambiguationData":[TD([[makeQuery(id+"F2.imprint","IMPRINT",EDGE,{"derivedFrom":sQuery(id+"F2.wireOp",EDGE,"E156.MirrorCS")}),1.0]])]});
            var Q10;
            Q10=makeQuery(id+"F2.imprint","IMPRINT",FACE,{"disambiguationData":[TD([[makeQuery(id+"F2.imprint","IMPRINT",EDGE,{"derivedFrom":sQuery(id+"F2.wireOp",EDGE,"E188.MirrorCS")}),-1.0]])]});
            var Q11;
            Q11=makeQuery(id+"F2.imprint","IMPRINT",FACE,{"disambiguationData":[TD([[makeQuery(id+"F2.imprint","IMPRINT",EDGE,{"derivedFrom":sQuery(id+"F2.wireOp",EDGE,"E184.MirrorCS")}),-1.0]])]});
            var Q12;
            Q12=makeQuery(id+"F2.imprint","IMPRINT",FACE,{"disambiguationData":[TD([[makeQuery(id+"F2.imprint","IMPRINT",EDGE,{"derivedFrom":sQuery(id+"F2.wireOp",EDGE,"E181.MirrorCS")}),1.0]])]});
            var Q13;
            Q13=makeQuery(id+"F2.imprint","IMPRINT",FACE,{"disambiguationData":[TD([[makeQuery(id+"F2.imprint","IMPRINT",EDGE,{"derivedFrom":sQuery(id+"F2.wireOp",EDGE,"E178.MirrorCS")}),-1.0]])]});
            var Q14;
            Q14=makeQuery(id+"F2.imprint","IMPRINT",FACE,{"disambiguationData":[TD([[makeQuery(id+"F2.imprint","IMPRINT",EDGE,{"derivedFrom":sQuery(id+"F2.wireOp",EDGE,"E173.MirrorCS")}),-1.0]])]});
            var Q15;
            Q15=makeQuery(id+"F2.imprint","IMPRINT",FACE,{"disambiguationData":[TD([[makeQuery(id+"F2.imprint","IMPRINT",EDGE,{"derivedFrom":sQuery(id+"F2.wireOp",EDGE,"E175.MirrorCS")}),1.0]])]});
            var Q16;
            Q16=makeQuery(id+"F2.imprint","IMPRINT",FACE,{"disambiguationData":[TD([[makeQuery(id+"F2.imprint","IMPRINT",EDGE,{"derivedFrom":sQuery(id+"F2.wireOp",EDGE,"E174.MirrorCS")}),-1.0]])]});
            var Q17;
            Q17=makeQuery(id+"F2.imprint","IMPRINT",FACE,{"disambiguationData":[TD([[makeQuery(id+"F2.imprint","IMPRINT",EDGE,{"derivedFrom":sQuery(id+"F2.wireOp",EDGE,"E172.MirrorCS")}),-1.0]])]});
            var Q18;
            Q18=makeQuery(id+"F2.imprint","IMPRINT",FACE,{"disambiguationData":[TD([[makeQuery(id+"F2.imprint","IMPRINT",EDGE,{"derivedFrom":sQuery(id+"F2.wireOp",EDGE,"E183.MirrorCS")}),1.0]])]});
            var Q19;
            {var subQ8=sQuery(id+"F2.wireOp",EDGE,"E202.MirrorCS");Q19=makeQuery(id+"F2.imprint","IMPRINT",FACE,{"disambiguationData":[TD([[makeQuery(id+"F2.imprint","IMPRINT",EDGE,{"derivedFrom":subQ8}),1.0]])]});}
            var Q20;
            Q20=makeQuery(id+"F2.imprint","IMPRINT",FACE,{"disambiguationData":[TD([[makeQuery(id+"F2.imprint","IMPRINT",EDGE,{"derivedFrom":sQuery(id+"F2.wireOp",EDGE,"E192.MirrorCS")}),1.0]])]});
            var Q21;
            Q21=makeQuery(id+"F2.imprint","IMPRINT",FACE,{"disambiguationData":[TD([[makeQuery(id+"F2.imprint","IMPRINT",EDGE,{"derivedFrom":sQuery(id+"F2.wireOp",EDGE,"E164.MirrorCS")}),1.0]])]});
            var Q22;
            {var subQ7=sQuery(id+"F2.wireOp",EDGE,"E167");Q22=makeQuery(id+"F2.imprint","IMPRINT",FACE,{"disambiguationData":[TD([[makeQuery(id+"F2.imprint","IMPRINT",EDGE,{"derivedFrom":subQ7}),1.0]])]});}
            extrude(context, id + "F4", {"entities" : qUnion([Q0, Q1, Q2, Q3, Q4, Q5, Q6, Q7, Q8, Q9, Q10, Q11, Q12, Q13, Q14, Q15, Q16, Q17, Q18, Q19, Q20, Q21, Q22]), "endBound" : BoundingType.SYMMETRIC, "depth" : 40 * mm, "offsetDistance" : 25 * mm});
        }
        {
            var Q0;
            Q0=qCreatedBy(id+"F3.planeOp",FACE);
            var sketch = newSketch(context, id + "F5", { "sketchPlane" : qUnion([Q0])});
            skLineSegment(sketch, "E244.0", {"start": v(-2194.22, 0) * mm, "end": v(2196.22, 0) * mm, "construction": true});
            skLineSegment(sketch, "E244.1", {"start": v(0, 0.48) * mm, "end": v(0, -0.7) * mm, "construction": true});
            skLineSegment(sketch, "E244.2", {"start": v(0, 760) * mm, "end": v(438.79, 0) * mm, "construction": true});
            skLineSegment(sketch, "E244.3", {"start": v(438.79, 0) * mm, "end": v(877.57, 760) * mm, "construction": true});
            skLineSegment(sketch, "E244.4", {"start": v(0, 760) * mm, "end": v(877.57, 760) * mm, "construction": true});
            skLineSegment(sketch, "E244.5", {"start": v(877.57, 760) * mm, "end": v(877.57, 744.9) * mm, "construction": true});
            skLineSegment(sketch, "E244.6", {"start": v(1316.36, 0) * mm, "end": v(877.57, 760) * mm, "construction": true});
            skLineSegment(sketch, "E244.7", {"start": v(1755.14, 760) * mm, "end": v(1316.36, 0) * mm, "construction": true});
            skLineSegment(sketch, "E244.8", {"start": v(1755.14, 760) * mm, "end": v(877.57, 760) * mm, "construction": true});
            skLineSegment(sketch, "E244.9", {"start": v(1755.14, 760) * mm, "end": v(1755.14, 750.7) * mm, "construction": true});
            skLineSegment(sketch, "E244.10", {"start": v(1755.14, 760) * mm, "end": v(2193.93, 0) * mm, "construction": true});
            skLineSegment(sketch, "E244.19", {"start": v(0, 760) * mm, "end": v(-438.79, 0) * mm, "construction": true});
            skLineSegment(sketch, "E244.20", {"start": v(-438.79, 0) * mm, "end": v(-877.57, 760) * mm, "construction": true});
            skLineSegment(sketch, "E244.21", {"start": v(0, 760) * mm, "end": v(-877.57, 760) * mm, "construction": true});
            skLineSegment(sketch, "E244.22", {"start": v(-877.57, 760) * mm, "end": v(-877.57, 744.9) * mm, "construction": true});
            skLineSegment(sketch, "E244.24", {"start": v(-1755.14, 760) * mm, "end": v(-1755.14, 750.7) * mm, "construction": true});
            skLineSegment(sketch, "E244.25", {"start": v(-1316.36, 0) * mm, "end": v(-877.57, 760) * mm, "construction": true});
            skLineSegment(sketch, "E244.26", {"start": v(-1755.14, 760) * mm, "end": v(-877.57, 760) * mm, "construction": true});
            skLineSegment(sketch, "E244.28", {"start": v(-1755.14, 760) * mm, "end": v(-1316.36, 0) * mm, "construction": true});
            skLineSegment(sketch, "E244.32", {"start": v(-1755.14, 760) * mm, "end": v(-2193.93, 0) * mm, "construction": true});
            skCircle(sketch, "E244.34", {"center": v(438.79, 760) * mm, "radius": 380 * mm, "construction": true});
            skLineSegment(sketch, "E244.37", {"start": v(1316.36, 0) * mm, "end": v(1316.36, -2.45) * mm, "construction": true});
            skCircle(sketch, "E244.39", {"center": v(1316.36, 760) * mm, "radius": 380 * mm, "construction": true});
            skCircle(sketch, "E244.42", {"center": v(-438.79, 760) * mm, "radius": 380 * mm, "construction": true});
            skCircle(sketch, "E244.43", {"center": v(-1316.36, 760) * mm, "radius": 380 * mm, "construction": true});
            skLineSegment(sketch, "E244.48", {"start": v(0, 1140) * mm, "end": v(1535.75, 1140) * mm, "construction": true});
            skLineSegment(sketch, "E244.49", {"start": v(1535.75, 1140) * mm, "end": v(1755.14, 760) * mm, "construction": true});
            skLineSegment(sketch, "E244.52", {"start": v(0, 1140) * mm, "end": v(-1535.75, 1140) * mm, "construction": true});
            skLineSegment(sketch, "E244.53", {"start": v(-1535.75, 1140) * mm, "end": v(-1755.14, 760) * mm, "construction": true});
            skLineSegment(sketch, "E244.54", {"start": v(0, 1140) * mm, "end": v(-1535.75, 1140) * mm, "construction": true});
            skLineSegment(sketch, "E244.55", {"start": v(-1535.75, 1140) * mm, "end": v(-1755.14, 760) * mm, "construction": true});
            skLineSegment(sketch, "E245", {"start": v(-1542.25, 1128.75) * mm, "end": v(-1535.75, 1125) * mm});
            skLineSegment(sketch, "E246", {"start": v(-1535.75, 1125) * mm, "end": v(-1742.15, 767.5) * mm});
            skLineSegment(sketch, "E247", {"start": v(-1742.15, 767.5) * mm, "end": v(-1748.65, 771.25) * mm});
            skLineSegment(sketch, "E248.MirrorCS", {"start": v(-1542.25, 1128.75) * mm, "end": v(-1548.74, 1132.5) * mm});
            skLineSegment(sketch, "E249.MirrorCS", {"start": v(-1548.74, 1132.5) * mm, "end": v(-1755.14, 775) * mm});
            skLineSegment(sketch, "E250.MirrorCS", {"start": v(-1755.14, 775) * mm, "end": v(-1748.65, 771.25) * mm});
            skLineSegment(sketch, "E251", {"start": v(-871.08, 771.25) * mm, "end": v(-877.57, 775) * mm});
            skLineSegment(sketch, "E252", {"start": v(-877.57, 775) * mm, "end": v(-671.17, 1132.5) * mm});
            skLineSegment(sketch, "E253", {"start": v(-671.17, 1132.5) * mm, "end": v(-664.67, 1128.75) * mm});
            skLineSegment(sketch, "E254.MirrorCS", {"start": v(-871.08, 771.25) * mm, "end": v(-864.58, 767.5) * mm});
            skLineSegment(sketch, "E255.MirrorCS", {"start": v(-864.58, 767.5) * mm, "end": v(-658.18, 1125) * mm});
            skLineSegment(sketch, "E256.MirrorCS", {"start": v(-658.18, 1125) * mm, "end": v(-664.67, 1128.75) * mm});
            skLineSegment(sketch, "E257", {"start": v(-877.57, 760) * mm, "end": v(-664.67, 1128.75) * mm, "construction": true});
            skLineSegment(sketch, "E258", {"start": v(-1768.14, 760) * mm, "end": v(-1768.14, 767.5) * mm});
            skLineSegment(sketch, "E259", {"start": v(-1768.14, 767.5) * mm, "end": v(0, 767.5) * mm});
            skLineSegment(sketch, "E260.MirrorCS", {"start": v(-1768.14, 760) * mm, "end": v(-1768.14, 752.5) * mm});
            skLineSegment(sketch, "E261.MirrorCS", {"start": v(-1768.14, 752.5) * mm, "end": v(0, 752.5) * mm});
            skPoint(sketch, "E262.MirrorCS.end.orphan", {"position": v(0, 760) * mm});
            skPoint(sketch, "E262.MirrorCS.start.orphan", {"position": v(0, 752.5) * mm});
            skLineSegment(sketch, "E263", {"start": v(-2187.44, 11.25) * mm, "end": v(-2193.93, 15) * mm});
            skLineSegment(sketch, "E264", {"start": v(-2193.93, 15) * mm, "end": v(-1768.14, 752.5) * mm});
            skLineSegment(sketch, "E265", {"start": v(-1768.14, 752.5) * mm, "end": v(-1761.64, 748.75) * mm});
            skLineSegment(sketch, "E266.MirrorCS", {"start": v(-1755.14, 745) * mm, "end": v(-1761.64, 748.75) * mm});
            skLineSegment(sketch, "E267.MirrorCS", {"start": v(-2180.94, 7.5) * mm, "end": v(-1755.14, 745) * mm});
            skLineSegment(sketch, "E268.MirrorCS", {"start": v(-2187.44, 11.25) * mm, "end": v(-2180.94, 7.5) * mm});
            skLineSegment(sketch, "E269", {"start": v(-2198.26, 0) * mm, "end": v(-2198.26, 7.5) * mm});
            skLineSegment(sketch, "E270", {"start": v(-2198.26, 7.5) * mm, "end": v(0, 7.5) * mm});
            skLineSegment(sketch, "E271", {"start": v(-2193.93, 15) * mm, "end": v(-2198.26, 7.5) * mm, "construction": true});
            skLineSegment(sketch, "E272.MirrorCS", {"start": v(-1329.35, 7.5) * mm, "end": v(-1755.14, 745) * mm});
            skLineSegment(sketch, "E273.MirrorCS", {"start": v(-1755.14, 745) * mm, "end": v(-1748.65, 748.75) * mm});
            skLineSegment(sketch, "E274.MirrorCS", {"start": v(-1742.15, 752.5) * mm, "end": v(-1748.65, 748.75) * mm});
            skLineSegment(sketch, "E275.MirrorCS", {"start": v(-1316.36, 15) * mm, "end": v(-1742.15, 752.5) * mm});
            skLineSegment(sketch, "E276.MirrorCS", {"start": v(-1322.85, 11.25) * mm, "end": v(-1316.36, 15) * mm});
            skLineSegment(sketch, "E277.MirrorCS", {"start": v(-1322.85, 11.25) * mm, "end": v(-1329.35, 7.5) * mm});
            skLineSegment(sketch, "E278", {"start": v(-1316.36, 0) * mm, "end": v(-1316.36, 7.5) * mm, "construction": true});
            skLineSegment(sketch, "E279.MirrorCS", {"start": v(-1303.37, 7.5) * mm, "end": v(-877.57, 745) * mm});
            skLineSegment(sketch, "E280.MirrorCS", {"start": v(-1309.86, 11.25) * mm, "end": v(-1303.37, 7.5) * mm});
            skLineSegment(sketch, "E281.MirrorCS", {"start": v(-1309.86, 11.25) * mm, "end": v(-1316.36, 15) * mm});
            skLineSegment(sketch, "E282.MirrorCS", {"start": v(-1316.36, 15) * mm, "end": v(-890.56, 752.5) * mm});
            skLineSegment(sketch, "E283.MirrorCS", {"start": v(-877.57, 745) * mm, "end": v(-884.07, 748.75) * mm});
            skLineSegment(sketch, "E284.MirrorCS", {"start": v(-890.56, 752.5) * mm, "end": v(-884.07, 748.75) * mm});
            skLineSegment(sketch, "E285.MirrorCS", {"start": v(-451.78, 7.5) * mm, "end": v(-877.57, 745) * mm});
            skLineSegment(sketch, "E286.MirrorCS", {"start": v(-877.57, 745) * mm, "end": v(-871.08, 748.75) * mm});
            skLineSegment(sketch, "E287.MirrorCS", {"start": v(-864.58, 752.5) * mm, "end": v(-871.08, 748.75) * mm});
            skLineSegment(sketch, "E288.MirrorCS", {"start": v(-438.79, 15) * mm, "end": v(-864.58, 752.5) * mm});
            skLineSegment(sketch, "E289.MirrorCS", {"start": v(-445.28, 11.25) * mm, "end": v(-438.79, 15) * mm});
            skLineSegment(sketch, "E290.MirrorCS", {"start": v(-445.28, 11.25) * mm, "end": v(-451.78, 7.5) * mm});
            skLineSegment(sketch, "E291", {"start": v(-438.79, 0) * mm, "end": v(-438.79, 7.5) * mm, "construction": true});
            skLineSegment(sketch, "E292.MirrorCS", {"start": v(-438.79, 15) * mm, "end": v(-13, 752.5) * mm});
            skLineSegment(sketch, "E293.MirrorCS", {"start": v(-432.3, 11.25) * mm, "end": v(-438.79, 15) * mm});
            skLineSegment(sketch, "E294.MirrorCS", {"start": v(-432.3, 11.25) * mm, "end": v(-425.8, 7.5) * mm});
            skLineSegment(sketch, "E295.MirrorCS", {"start": v(-425.8, 7.5) * mm, "end": v(0, 745) * mm});
            skLineSegment(sketch, "E296.MirrorCS", {"start": v(0, 745) * mm, "end": v(-6.5, 748.75) * mm});
            skLineSegment(sketch, "E297.MirrorCS", {"start": v(-13, 752.5) * mm, "end": v(-6.5, 748.75) * mm});
            skLineSegment(sketch, "E298.MirrorCS", {"start": v(1768.14, 752.5) * mm, "end": v(0, 752.5) * mm});
            skLineSegment(sketch, "E299.MirrorCS", {"start": v(1768.14, 767.5) * mm, "end": v(0, 767.5) * mm});
            skLineSegment(sketch, "E300.MirrorCS", {"start": v(1768.14, 760) * mm, "end": v(1768.14, 767.5) * mm});
            skLineSegment(sketch, "E301.MirrorCS", {"start": v(1768.14, 760) * mm, "end": v(1768.14, 752.5) * mm});
            skLineSegment(sketch, "E302.MirrorCS", {"start": v(2198.26, 7.5) * mm, "end": v(0, 7.5) * mm});
            skLineSegment(sketch, "E303.MirrorCS", {"start": v(2198.26, 0) * mm, "end": v(2198.26, 7.5) * mm});
            skLineSegment(sketch, "E304.MirrorCS", {"start": v(2193.93, 15) * mm, "end": v(1768.14, 752.5) * mm});
            skLineSegment(sketch, "E305.MirrorCS", {"start": v(1768.14, 752.5) * mm, "end": v(1761.64, 748.75) * mm});
            skLineSegment(sketch, "E306.MirrorCS", {"start": v(1755.14, 745) * mm, "end": v(1761.64, 748.75) * mm});
            skLineSegment(sketch, "E307.MirrorCS", {"start": v(2180.94, 7.5) * mm, "end": v(1755.14, 745) * mm});
            skLineSegment(sketch, "E308.MirrorCS", {"start": v(1329.35, 7.5) * mm, "end": v(1755.14, 745) * mm});
            skLineSegment(sketch, "E309.MirrorCS", {"start": v(1755.14, 745) * mm, "end": v(1748.65, 748.75) * mm});
            skLineSegment(sketch, "E310.MirrorCS", {"start": v(1742.15, 752.5) * mm, "end": v(1748.65, 748.75) * mm});
            skLineSegment(sketch, "E311.MirrorCS", {"start": v(1316.36, 15) * mm, "end": v(1742.15, 752.5) * mm});
            skLineSegment(sketch, "E312.MirrorCS", {"start": v(2187.44, 11.25) * mm, "end": v(2193.93, 15) * mm});
            skLineSegment(sketch, "E313.MirrorCS", {"start": v(2187.44, 11.25) * mm, "end": v(2180.94, 7.5) * mm});
            skLineSegment(sketch, "E314.MirrorCS", {"start": v(1322.85, 11.25) * mm, "end": v(1329.35, 7.5) * mm});
            skLineSegment(sketch, "E315.MirrorCS", {"start": v(1322.85, 11.25) * mm, "end": v(1316.36, 15) * mm});
            skLineSegment(sketch, "E316.MirrorCS", {"start": v(1309.86, 11.25) * mm, "end": v(1316.36, 15) * mm});
            skLineSegment(sketch, "E317.MirrorCS", {"start": v(1309.86, 11.25) * mm, "end": v(1303.37, 7.5) * mm});
            skLineSegment(sketch, "E318.MirrorCS", {"start": v(1303.37, 7.5) * mm, "end": v(877.57, 745) * mm});
            skLineSegment(sketch, "E319.MirrorCS", {"start": v(1316.36, 15) * mm, "end": v(890.56, 752.5) * mm});
            skLineSegment(sketch, "E320.MirrorCS", {"start": v(451.78, 7.5) * mm, "end": v(877.57, 745) * mm});
            skLineSegment(sketch, "E321.MirrorCS", {"start": v(445.28, 11.25) * mm, "end": v(451.78, 7.5) * mm});
            skLineSegment(sketch, "E322.MirrorCS", {"start": v(445.28, 11.25) * mm, "end": v(438.79, 15) * mm});
            skLineSegment(sketch, "E323.MirrorCS", {"start": v(438.79, 15) * mm, "end": v(864.58, 752.5) * mm});
            skLineSegment(sketch, "E324.MirrorCS", {"start": v(890.56, 752.5) * mm, "end": v(884.07, 748.75) * mm});
            skLineSegment(sketch, "E325.MirrorCS", {"start": v(877.57, 745) * mm, "end": v(884.07, 748.75) * mm});
            skLineSegment(sketch, "E326.MirrorCS", {"start": v(877.57, 745) * mm, "end": v(871.08, 748.75) * mm});
            skLineSegment(sketch, "E327.MirrorCS", {"start": v(864.58, 752.5) * mm, "end": v(871.08, 748.75) * mm});
            skLineSegment(sketch, "E328.MirrorCS", {"start": v(432.3, 11.25) * mm, "end": v(438.79, 15) * mm});
            skLineSegment(sketch, "E329.MirrorCS", {"start": v(432.3, 11.25) * mm, "end": v(425.8, 7.5) * mm});
            skLineSegment(sketch, "E330.MirrorCS", {"start": v(425.8, 7.5) * mm, "end": v(0, 745) * mm});
            skLineSegment(sketch, "E331.MirrorCS", {"start": v(438.79, 15) * mm, "end": v(13, 752.5) * mm});
            skLineSegment(sketch, "E332.MirrorCS", {"start": v(13, 752.5) * mm, "end": v(6.5, 748.75) * mm});
            skLineSegment(sketch, "E333.MirrorCS", {"start": v(0, 745) * mm, "end": v(6.5, 748.75) * mm});
            skLineSegment(sketch, "E334.MirrorCS", {"start": v(864.58, 767.5) * mm, "end": v(658.18, 1125) * mm});
            skLineSegment(sketch, "E335.MirrorCS", {"start": v(877.57, 775) * mm, "end": v(671.17, 1132.5) * mm});
            skLineSegment(sketch, "E336.MirrorCS", {"start": v(871.08, 771.25) * mm, "end": v(877.57, 775) * mm});
            skLineSegment(sketch, "E337.MirrorCS", {"start": v(871.08, 771.25) * mm, "end": v(864.58, 767.5) * mm});
            skLineSegment(sketch, "E338.MirrorCS", {"start": v(671.17, 1132.5) * mm, "end": v(664.67, 1128.75) * mm});
            skLineSegment(sketch, "E339.MirrorCS", {"start": v(658.18, 1125) * mm, "end": v(664.67, 1128.75) * mm});
            skLineSegment(sketch, "E340.MirrorCS", {"start": v(1535.75, 1125) * mm, "end": v(1742.15, 767.5) * mm});
            skLineSegment(sketch, "E341.MirrorCS", {"start": v(1742.15, 767.5) * mm, "end": v(1748.65, 771.25) * mm});
            skLineSegment(sketch, "E342.MirrorCS", {"start": v(1755.14, 775) * mm, "end": v(1748.65, 771.25) * mm});
            skLineSegment(sketch, "E343.MirrorCS", {"start": v(1548.74, 1132.5) * mm, "end": v(1755.14, 775) * mm});
            skLineSegment(sketch, "E344.MirrorCS", {"start": v(1542.25, 1128.75) * mm, "end": v(1548.74, 1132.5) * mm});
            skLineSegment(sketch, "E345.MirrorCS", {"start": v(1542.25, 1128.75) * mm, "end": v(1535.75, 1125) * mm});
            skLineSegment(sketch, "E346.MirrorCS", {"start": v(2193.93, 15) * mm, "end": v(2198.26, 7.5) * mm, "construction": true});
            skPoint(sketch, "E347.MirrorCS.start.orphan", {"position": v(2198.26, 0) * mm});
            skPoint(sketch, "E348.MirrorCS.end.orphan", {"position": v(0, -7.5) * mm});
            skPoint(sketch, "E349.MirrorCS.start.orphan", {"position": v(-2198.26, 0) * mm});
            skLineSegment(sketch, "E350.MirrorCS", {"start": v(-1542.25, -1128.75) * mm, "end": v(-1535.75, -1125) * mm});
            skLineSegment(sketch, "E351.MirrorCS", {"start": v(-877.57, -745) * mm, "end": v(-884.07, -748.75) * mm});
            skLineSegment(sketch, "E352.MirrorCS", {"start": v(-1768.14, -752.5) * mm, "end": v(-1761.64, -748.75) * mm});
            skLineSegment(sketch, "E353.MirrorCS", {"start": v(-877.57, -745) * mm, "end": v(-871.08, -748.75) * mm});
            skLineSegment(sketch, "E354.MirrorCS", {"start": v(-1542.25, -1128.75) * mm, "end": v(-1548.74, -1132.5) * mm});
            skLineSegment(sketch, "E355.MirrorCS", {"start": v(-1755.14, -775) * mm, "end": v(-1748.65, -771.25) * mm});
            skLineSegment(sketch, "E356.MirrorCS", {"start": v(-1755.14, -745) * mm, "end": v(-1761.64, -748.75) * mm});
            skLineSegment(sketch, "E357.MirrorCS", {"start": v(890.56, -752.5) * mm, "end": v(884.07, -748.75) * mm});
            skLineSegment(sketch, "E358.MirrorCS", {"start": v(-871.08, -771.25) * mm, "end": v(-877.57, -775) * mm});
            skLineSegment(sketch, "E359.MirrorCS", {"start": v(0, -745) * mm, "end": v(6.5, -748.75) * mm});
            skLineSegment(sketch, "E360.MirrorCS", {"start": v(-890.56, -752.5) * mm, "end": v(-884.07, -748.75) * mm});
            skLineSegment(sketch, "E361.MirrorCS", {"start": v(-864.58, -752.5) * mm, "end": v(-871.08, -748.75) * mm});
            skLineSegment(sketch, "E362.MirrorCS", {"start": v(-1755.14, -745) * mm, "end": v(-1748.65, -748.75) * mm});
            skLineSegment(sketch, "E363.MirrorCS", {"start": v(-1742.15, -767.5) * mm, "end": v(-1748.65, -771.25) * mm});
            skLineSegment(sketch, "E364.MirrorCS", {"start": v(-2198.26, 0) * mm, "end": v(-2198.26, -7.5) * mm});
            skLineSegment(sketch, "E365.MirrorCS", {"start": v(-877.57, -760) * mm, "end": v(-877.57, -744.9) * mm, "construction": true});
            skLineSegment(sketch, "E366.MirrorCS", {"start": v(-1755.14, -760) * mm, "end": v(-1755.14, -750.7) * mm, "construction": true});
            skLineSegment(sketch, "E367.MirrorCS", {"start": v(-871.08, -771.25) * mm, "end": v(-864.58, -767.5) * mm});
            skLineSegment(sketch, "E368.MirrorCS", {"start": v(-1742.15, -752.5) * mm, "end": v(-1748.65, -748.75) * mm});
            skLineSegment(sketch, "E369.MirrorCS", {"start": v(-1768.14, -760) * mm, "end": v(-1768.14, -752.5) * mm});
            skLineSegment(sketch, "E370.MirrorCS", {"start": v(871.08, -771.25) * mm, "end": v(864.58, -767.5) * mm});
            skLineSegment(sketch, "E371.MirrorCS", {"start": v(877.57, -745) * mm, "end": v(884.07, -748.75) * mm});
            skLineSegment(sketch, "E372.MirrorCS", {"start": v(0, -745) * mm, "end": v(-6.5, -748.75) * mm});
            skLineSegment(sketch, "E373.MirrorCS", {"start": v(-1768.14, -760) * mm, "end": v(-1768.14, -767.5) * mm});
            skLineSegment(sketch, "E374.MirrorCS", {"start": v(-1309.86, -11.25) * mm, "end": v(-1316.36, -15) * mm});
            skLineSegment(sketch, "E375.MirrorCS", {"start": v(877.57, -760) * mm, "end": v(877.57, -744.9) * mm, "construction": true});
            skLineSegment(sketch, "E376.MirrorCS", {"start": v(13, -752.5) * mm, "end": v(6.5, -748.75) * mm});
            skLineSegment(sketch, "E377.MirrorCS", {"start": v(1309.86, -11.25) * mm, "end": v(1303.37, -7.5) * mm});
            skLineSegment(sketch, "E378.MirrorCS", {"start": v(864.58, -752.5) * mm, "end": v(871.08, -748.75) * mm});
            skLineSegment(sketch, "E379.MirrorCS", {"start": v(-1322.85, -11.25) * mm, "end": v(-1316.36, -15) * mm});
            skLineSegment(sketch, "E380.MirrorCS", {"start": v(-2187.44, -11.25) * mm, "end": v(-2193.93, -15) * mm});
            skLineSegment(sketch, "E381.MirrorCS", {"start": v(877.57, -745) * mm, "end": v(871.08, -748.75) * mm});
            skLineSegment(sketch, "E382.MirrorCS", {"start": v(-13, -752.5) * mm, "end": v(-6.5, -748.75) * mm});
            skLineSegment(sketch, "E383.MirrorCS", {"start": v(1322.85, -11.25) * mm, "end": v(1329.35, -7.5) * mm});
            skLineSegment(sketch, "E384.MirrorCS", {"start": v(-2193.93, -15) * mm, "end": v(-2198.26, -7.5) * mm, "construction": true});
            skLineSegment(sketch, "E385.MirrorCS", {"start": v(-2187.44, -11.25) * mm, "end": v(-2180.94, -7.5) * mm});
            skLineSegment(sketch, "E386.MirrorCS", {"start": v(-445.28, -11.25) * mm, "end": v(-438.79, -15) * mm});
            skLineSegment(sketch, "E387.MirrorCS", {"start": v(871.08, -771.25) * mm, "end": v(877.57, -775) * mm});
            skLineSegment(sketch, "E388.MirrorCS", {"start": v(-1322.85, -11.25) * mm, "end": v(-1329.35, -7.5) * mm});
            skLineSegment(sketch, "E389.MirrorCS", {"start": v(1755.14, -775) * mm, "end": v(1748.65, -771.25) * mm});
            skLineSegment(sketch, "E390.MirrorCS", {"start": v(1742.15, -752.5) * mm, "end": v(1748.65, -748.75) * mm});
            skLineSegment(sketch, "E391.MirrorCS", {"start": v(-432.3, -11.25) * mm, "end": v(-438.79, -15) * mm});
            skLineSegment(sketch, "E392.MirrorCS", {"start": v(1322.85, -11.25) * mm, "end": v(1316.36, -15) * mm});
            skLineSegment(sketch, "E393.MirrorCS", {"start": v(1316.36, 0) * mm, "end": v(1316.36, 2.45) * mm, "construction": true});
            skLineSegment(sketch, "E394.MirrorCS", {"start": v(445.28, -11.25) * mm, "end": v(451.78, -7.5) * mm});
            skLineSegment(sketch, "E395.MirrorCS", {"start": v(1768.14, -752.5) * mm, "end": v(1761.64, -748.75) * mm});
            skLineSegment(sketch, "E396.MirrorCS", {"start": v(2198.26, 0) * mm, "end": v(2198.26, -7.5) * mm});
            skLineSegment(sketch, "E397.MirrorCS", {"start": v(1309.86, -11.25) * mm, "end": v(1316.36, -15) * mm});
            skLineSegment(sketch, "E398.MirrorCS", {"start": v(2187.44, -11.25) * mm, "end": v(2180.94, -7.5) * mm});
            skLineSegment(sketch, "E399.MirrorCS", {"start": v(1768.14, -760) * mm, "end": v(1768.14, -752.5) * mm});
            skLineSegment(sketch, "E400.MirrorCS", {"start": v(-438.79, 0) * mm, "end": v(-438.79, -7.5) * mm, "construction": true});
            skLineSegment(sketch, "E401.MirrorCS", {"start": v(1755.14, -760) * mm, "end": v(1755.14, -750.7) * mm, "construction": true});
            skLineSegment(sketch, "E402.MirrorCS", {"start": v(1768.14, -760) * mm, "end": v(1768.14, -767.5) * mm});
            skLineSegment(sketch, "E403.MirrorCS", {"start": v(-1309.86, -11.25) * mm, "end": v(-1303.37, -7.5) * mm});
            skLineSegment(sketch, "E404.MirrorCS", {"start": v(1755.14, -745) * mm, "end": v(1748.65, -748.75) * mm});
            skLineSegment(sketch, "E405.MirrorCS", {"start": v(1742.15, -767.5) * mm, "end": v(1748.65, -771.25) * mm});
            skLineSegment(sketch, "E406.MirrorCS", {"start": v(-432.3, -11.25) * mm, "end": v(-425.8, -7.5) * mm});
            skLineSegment(sketch, "E407.MirrorCS", {"start": v(2187.44, -11.25) * mm, "end": v(2193.93, -15) * mm});
            skLineSegment(sketch, "E408.MirrorCS", {"start": v(1755.14, -745) * mm, "end": v(1761.64, -748.75) * mm});
            skLineSegment(sketch, "E409.MirrorCS", {"start": v(-445.28, -11.25) * mm, "end": v(-451.78, -7.5) * mm});
            skLineSegment(sketch, "E410.MirrorCS", {"start": v(2193.93, -15) * mm, "end": v(2198.26, -7.5) * mm, "construction": true});
            skLineSegment(sketch, "E411.MirrorCS", {"start": v(432.3, -11.25) * mm, "end": v(438.79, -15) * mm});
            skLineSegment(sketch, "E412.MirrorCS", {"start": v(-1316.36, 0) * mm, "end": v(-1316.36, -7.5) * mm, "construction": true});
            skLineSegment(sketch, "E413.MirrorCS", {"start": v(445.28, -11.25) * mm, "end": v(438.79, -15) * mm});
            skLineSegment(sketch, "E414.MirrorCS", {"start": v(432.3, -11.25) * mm, "end": v(425.8, -7.5) * mm});
            skLineSegment(sketch, "E415.MirrorCS", {"start": v(1542.25, -1128.75) * mm, "end": v(1548.74, -1132.5) * mm});
            skLineSegment(sketch, "E416.MirrorCS", {"start": v(1542.25, -1128.75) * mm, "end": v(1535.75, -1125) * mm});
            skLineSegment(sketch, "E417.MirrorCS", {"start": v(-671.17, -1132.5) * mm, "end": v(-664.67, -1128.75) * mm});
            skLineSegment(sketch, "E418.MirrorCS", {"start": v(-658.18, -1125) * mm, "end": v(-664.67, -1128.75) * mm});
            skLineSegment(sketch, "E419.MirrorCS", {"start": v(671.17, -1132.5) * mm, "end": v(664.67, -1128.75) * mm});
            skLineSegment(sketch, "E420.MirrorCS", {"start": v(0, -0.48) * mm, "end": v(0, 0.7) * mm, "construction": true});
            skLineSegment(sketch, "E421.MirrorCS", {"start": v(658.18, -1125) * mm, "end": v(664.67, -1128.75) * mm});
            skLineSegment(sketch, "E422.MirrorCS", {"start": v(1768.14, -767.5) * mm, "end": v(0, -767.5) * mm});
            skLineSegment(sketch, "E423.MirrorCS", {"start": v(0, -1140) * mm, "end": v(-1535.75, -1140) * mm, "construction": true});
            skLineSegment(sketch, "E424.MirrorCS", {"start": v(-1768.14, -767.5) * mm, "end": v(0, -767.5) * mm});
            skLineSegment(sketch, "E425.MirrorCS", {"start": v(-1535.75, -1125) * mm, "end": v(-1742.15, -767.5) * mm});
            skLineSegment(sketch, "E426.MirrorCS", {"start": v(-1535.75, -1140) * mm, "end": v(-1755.14, -760) * mm, "construction": true});
            skPoint(sketch, "E427.MirrorP", {"position": v(0, 7.5) * mm});
            skLineSegment(sketch, "E428.MirrorCS", {"start": v(425.8, -7.5) * mm, "end": v(0, -745) * mm});
            skLineSegment(sketch, "E429.MirrorCS", {"start": v(-1755.14, -760) * mm, "end": v(-1316.36, 0) * mm, "construction": true});
            skLineSegment(sketch, "E430.MirrorCS", {"start": v(-1768.14, -752.5) * mm, "end": v(0, -752.5) * mm});
            skLineSegment(sketch, "E431.MirrorCS", {"start": v(-438.79, 0) * mm, "end": v(-877.57, -760) * mm, "construction": true});
            skLineSegment(sketch, "E432.MirrorCS", {"start": v(-1303.37, -7.5) * mm, "end": v(-877.57, -745) * mm});
            skLineSegment(sketch, "E433.MirrorCS", {"start": v(-1329.35, -7.5) * mm, "end": v(-1755.14, -745) * mm});
            skLineSegment(sketch, "E434.MirrorCS", {"start": v(-2180.94, -7.5) * mm, "end": v(-1755.14, -745) * mm});
            skLineSegment(sketch, "E435.MirrorCS", {"start": v(2193.93, -15) * mm, "end": v(1768.14, -752.5) * mm});
            skLineSegment(sketch, "E436.MirrorCS", {"start": v(-425.8, -7.5) * mm, "end": v(0, -745) * mm});
            skLineSegment(sketch, "E437.MirrorCS", {"start": v(877.57, -775) * mm, "end": v(671.17, -1132.5) * mm});
            skLineSegment(sketch, "E438.MirrorCS", {"start": v(-1316.36, -15) * mm, "end": v(-890.56, -752.5) * mm});
            skLineSegment(sketch, "E439.MirrorCS", {"start": v(-1755.14, -760) * mm, "end": v(-877.57, -760) * mm, "construction": true});
            skLineSegment(sketch, "E440.MirrorCS", {"start": v(-1316.36, 0) * mm, "end": v(-877.57, -760) * mm, "construction": true});
            skLineSegment(sketch, "E441.MirrorCS", {"start": v(-451.78, -7.5) * mm, "end": v(-877.57, -745) * mm});
            skLineSegment(sketch, "E442.MirrorCS", {"start": v(0, -760) * mm, "end": v(877.57, -760) * mm, "construction": true});
            skCircle(sketch, "E443.MirrorC", {"center": v(-438.79, -760) * mm, "radius": 380 * mm, "construction": true});
            skLineSegment(sketch, "E444.MirrorCS", {"start": v(-864.58, -767.5) * mm, "end": v(-658.18, -1125) * mm});
            skLineSegment(sketch, "E445.MirrorCS", {"start": v(438.79, 0) * mm, "end": v(877.57, -760) * mm, "construction": true});
            skLineSegment(sketch, "E446.MirrorCS", {"start": v(1303.37, -7.5) * mm, "end": v(877.57, -745) * mm});
            skCircle(sketch, "E447.MirrorC", {"center": v(438.79, -760) * mm, "radius": 380 * mm, "construction": true});
            skLineSegment(sketch, "E448.MirrorCS", {"start": v(1548.74, -1132.5) * mm, "end": v(1755.14, -775) * mm});
            skLineSegment(sketch, "E449.MirrorCS", {"start": v(864.58, -767.5) * mm, "end": v(658.18, -1125) * mm});
            skLineSegment(sketch, "E450.MirrorCS", {"start": v(-438.79, -15) * mm, "end": v(-864.58, -752.5) * mm});
            skLineSegment(sketch, "E451.MirrorCS", {"start": v(-438.79, -15) * mm, "end": v(-13, -752.5) * mm});
            skLineSegment(sketch, "E452.MirrorCS", {"start": v(0, -760) * mm, "end": v(438.79, 0) * mm, "construction": true});
            skLineSegment(sketch, "E453.MirrorCS", {"start": v(1316.36, -15) * mm, "end": v(890.56, -752.5) * mm});
            skLineSegment(sketch, "E454.MirrorCS", {"start": v(1755.14, -760) * mm, "end": v(2193.93, 0) * mm, "construction": true});
            skLineSegment(sketch, "E455.MirrorCS", {"start": v(0, -760) * mm, "end": v(-438.79, 0) * mm, "construction": true});
            skLineSegment(sketch, "E456.MirrorCS", {"start": v(451.78, -7.5) * mm, "end": v(877.57, -745) * mm});
            skLineSegment(sketch, "E457.MirrorCS", {"start": v(-1548.74, -1132.5) * mm, "end": v(-1755.14, -775) * mm});
            skLineSegment(sketch, "E458.MirrorCS", {"start": v(1755.14, -760) * mm, "end": v(877.57, -760) * mm, "construction": true});
            skLineSegment(sketch, "E459.MirrorCS", {"start": v(-877.57, -775) * mm, "end": v(-671.17, -1132.5) * mm});
            skPoint(sketch, "E460.MirrorP", {"position": v(0, -752.5) * mm});
            skLineSegment(sketch, "E461.MirrorCS", {"start": v(1535.75, -1140) * mm, "end": v(1755.14, -760) * mm, "construction": true});
            skLineSegment(sketch, "E462.MirrorCS", {"start": v(-1755.14, -760) * mm, "end": v(-2193.93, 0) * mm, "construction": true});
            skLineSegment(sketch, "E463.MirrorCS", {"start": v(0, -1140) * mm, "end": v(1535.75, -1140) * mm, "construction": true});
            skLineSegment(sketch, "E464.MirrorCS", {"start": v(1316.36, 0) * mm, "end": v(877.57, -760) * mm, "construction": true});
            skLineSegment(sketch, "E465.MirrorCS", {"start": v(-877.57, -760) * mm, "end": v(-664.67, -1128.75) * mm, "construction": true});
            skCircle(sketch, "E466.MirrorC", {"center": v(-1316.36, -760) * mm, "radius": 380 * mm, "construction": true});
            skLineSegment(sketch, "E467.MirrorCS", {"start": v(1768.14, -752.5) * mm, "end": v(0, -752.5) * mm});
            skPoint(sketch, "E468.MirrorP", {"position": v(0, -760) * mm});
            skLineSegment(sketch, "E469.MirrorCS", {"start": v(438.79, -15) * mm, "end": v(13, -752.5) * mm});
            skLineSegment(sketch, "E470.MirrorCS", {"start": v(-2198.26, -7.5) * mm, "end": v(0, -7.5) * mm});
            skLineSegment(sketch, "E471.MirrorCS", {"start": v(1755.14, -760) * mm, "end": v(1316.36, 0) * mm, "construction": true});
            skLineSegment(sketch, "E472.MirrorCS", {"start": v(438.79, -15) * mm, "end": v(864.58, -752.5) * mm});
            skLineSegment(sketch, "E473.MirrorCS", {"start": v(1329.35, -7.5) * mm, "end": v(1755.14, -745) * mm});
            skLineSegment(sketch, "E474.MirrorCS", {"start": v(2180.94, -7.5) * mm, "end": v(1755.14, -745) * mm});
            skLineSegment(sketch, "E475.MirrorCS", {"start": v(2198.26, -7.5) * mm, "end": v(0, -7.5) * mm});
            skLineSegment(sketch, "E476.MirrorCS", {"start": v(1316.36, -15) * mm, "end": v(1742.15, -752.5) * mm});
            skLineSegment(sketch, "E477.MirrorCS", {"start": v(-2193.93, -15) * mm, "end": v(-1768.14, -752.5) * mm});
            skCircle(sketch, "E478.MirrorC", {"center": v(1316.36, -760) * mm, "radius": 380 * mm, "construction": true});
            skLineSegment(sketch, "E479.MirrorCS", {"start": v(1535.75, -1125) * mm, "end": v(1742.15, -767.5) * mm});
            skLineSegment(sketch, "E480.MirrorCS", {"start": v(-1316.36, -15) * mm, "end": v(-1742.15, -752.5) * mm});
            skLineSegment(sketch, "E481.MirrorCS", {"start": v(0, -760) * mm, "end": v(-877.57, -760) * mm, "construction": true});
            skLineSegment(sketch, "E482", {"start": v(0, 1140) * mm, "end": v(0, 1147.5) * mm});
            skLineSegment(sketch, "E483", {"start": v(0, 1147.5) * mm, "end": v(-1548.74, 1147.5) * mm});
            skLineSegment(sketch, "E484", {"start": v(-1548.74, 1147.5) * mm, "end": v(-1548.74, 1140) * mm});
            skLineSegment(sketch, "E485.MirrorCS", {"start": v(-1548.74, 1132.5) * mm, "end": v(-1548.74, 1140) * mm});
            skLineSegment(sketch, "E486.MirrorCS", {"start": v(0, 1132.5) * mm, "end": v(-1548.74, 1132.5) * mm});
            skLineSegment(sketch, "E487.MirrorCS", {"start": v(0, 1140) * mm, "end": v(0, 1132.5) * mm});
            skLineSegment(sketch, "E488.MirrorCS", {"start": v(1548.74, 1132.5) * mm, "end": v(1548.74, 1140) * mm});
            skLineSegment(sketch, "E489.MirrorCS", {"start": v(1548.74, 1147.5) * mm, "end": v(1548.74, 1140) * mm});
            skLineSegment(sketch, "E490.MirrorCS", {"start": v(0, 1147.5) * mm, "end": v(1548.74, 1147.5) * mm});
            skLineSegment(sketch, "E491.MirrorCS", {"start": v(0, 1132.5) * mm, "end": v(1548.74, 1132.5) * mm});
            skLineSegment(sketch, "E492.MirrorCS", {"start": v(-1548.74, -1132.5) * mm, "end": v(-1548.74, -1140) * mm});
            skLineSegment(sketch, "E493.MirrorCS", {"start": v(-1548.74, -1147.5) * mm, "end": v(-1548.74, -1140) * mm});
            skLineSegment(sketch, "E494.MirrorCS", {"start": v(0, -1147.5) * mm, "end": v(-1548.74, -1147.5) * mm});
            skLineSegment(sketch, "E495.MirrorCS", {"start": v(0, -1132.5) * mm, "end": v(-1548.74, -1132.5) * mm});
            skLineSegment(sketch, "E496.MirrorCS", {"start": v(0, -1147.5) * mm, "end": v(1548.74, -1147.5) * mm});
            skLineSegment(sketch, "E497.MirrorCS", {"start": v(0, -1132.5) * mm, "end": v(1548.74, -1132.5) * mm});
            skLineSegment(sketch, "E498.MirrorCS", {"start": v(1548.74, -1147.5) * mm, "end": v(1548.74, -1140) * mm});
            skLineSegment(sketch, "E499.MirrorCS", {"start": v(1548.74, -1132.5) * mm, "end": v(1548.74, -1140) * mm});
            skSolve(sketch);
        }
        {
            var Q0;
            {var subQ17=sQuery(id+"F5.wireOp",EDGE,"E269");Q0=makeQuery(id+"F5.imprint","IMPRINT",FACE,{"disambiguationData":[TD([[makeQuery(id+"F5.imprint","IMPRINT",EDGE,{"derivedFrom":subQ17}),-1.0]])]});}
            var Q1;
            Q1=makeQuery(id+"F5.imprint","IMPRINT",FACE,{"disambiguationData":[TD([[makeQuery(id+"F5.imprint","IMPRINT",EDGE,{"derivedFrom":sQuery(id+"F5.wireOp",EDGE,"E263")}),-1.0]])]});
            var Q2;
            Q2=makeQuery(id+"F5.imprint","IMPRINT",FACE,{"disambiguationData":[TD([[makeQuery(id+"F5.imprint","IMPRINT",EDGE,{"derivedFrom":sQuery(id+"F5.wireOp",EDGE,"E272.MirrorCS")}),-1.0]])]});
            var Q3;
            Q3=makeQuery(id+"F5.imprint","IMPRINT",FACE,{"disambiguationData":[TD([[makeQuery(id+"F5.imprint","IMPRINT",EDGE,{"derivedFrom":sQuery(id+"F5.wireOp",EDGE,"E279.MirrorCS")}),1.0]])]});
            var Q4;
            Q4=makeQuery(id+"F5.imprint","IMPRINT",FACE,{"disambiguationData":[TD([[makeQuery(id+"F5.imprint","IMPRINT",EDGE,{"derivedFrom":sQuery(id+"F5.wireOp",EDGE,"E285.MirrorCS")}),-1.0]])]});
            var Q5;
            Q5=makeQuery(id+"F5.imprint","IMPRINT",FACE,{"disambiguationData":[TD([[makeQuery(id+"F5.imprint","IMPRINT",EDGE,{"derivedFrom":sQuery(id+"F5.wireOp",EDGE,"E245")}),-1.0]])]});
            var Q6;
            {var subQ13=sQuery(id+"F5.wireOp",EDGE,"E258");Q6=makeQuery(id+"F5.imprint","IMPRINT",FACE,{"disambiguationData":[TD([[makeQuery(id+"F5.imprint","IMPRINT",EDGE,{"derivedFrom":subQ13}),-1.0]])]});}
            var Q7;
            Q7=makeQuery(id+"F5.imprint","IMPRINT",FACE,{"disambiguationData":[TD([[makeQuery(id+"F5.imprint","IMPRINT",EDGE,{"derivedFrom":sQuery(id+"F5.wireOp",EDGE,"jD5TgONc-o5aO-Mwn6-jDDA-3cEzYcpxTOwf")}),-1.0]])]});
            var Q8;
            Q8=makeQuery(id+"F5.imprint","IMPRINT",FACE,{"disambiguationData":[TD([[makeQuery(id+"F5.imprint","IMPRINT",EDGE,{"derivedFrom":sQuery(id+"F5.wireOp",EDGE,"E251")}),-1.0]])]});
            var Q9;
            Q9=makeQuery(id+"F5.imprint","IMPRINT",FACE,{"disambiguationData":[TD([[makeQuery(id+"F5.imprint","IMPRINT",EDGE,{"derivedFrom":sQuery(id+"F5.wireOp",EDGE,"E292.MirrorCS")}),-1.0]])]});
            var Q10;
            Q10=makeQuery(id+"F5.imprint","IMPRINT",FACE,{"disambiguationData":[TD([[makeQuery(id+"F5.imprint","IMPRINT",EDGE,{"derivedFrom":sQuery(id+"F5.wireOp",EDGE,"E328.MirrorCS")}),1.0]])]});
            var Q11;
            Q11=makeQuery(id+"F5.imprint","IMPRINT",FACE,{"disambiguationData":[TD([[makeQuery(id+"F5.imprint","IMPRINT",EDGE,{"derivedFrom":sQuery(id+"F5.wireOp",EDGE,"E334.MirrorCS")}),-1.0]])]});
            var Q12;
            Q12=makeQuery(id+"F5.imprint","IMPRINT",FACE,{"disambiguationData":[TD([[makeQuery(id+"F5.imprint","IMPRINT",EDGE,{"derivedFrom":sQuery(id+"F5.wireOp",EDGE,"E340.MirrorCS")}),1.0]])]});
            var Q13;
            Q13=makeQuery(id+"F5.imprint","IMPRINT",FACE,{"disambiguationData":[TD([[makeQuery(id+"F5.imprint","IMPRINT",EDGE,{"derivedFrom":sQuery(id+"F5.wireOp",EDGE,"E308.MirrorCS")}),1.0]])]});
            var Q14;
            Q14=makeQuery(id+"F5.imprint","IMPRINT",FACE,{"disambiguationData":[TD([[makeQuery(id+"F5.imprint","IMPRINT",EDGE,{"derivedFrom":sQuery(id+"F5.wireOp",EDGE,"E316.MirrorCS")}),1.0]])]});
            var Q15;
            Q15=makeQuery(id+"F5.imprint","IMPRINT",FACE,{"disambiguationData":[TD([[makeQuery(id+"F5.imprint","IMPRINT",EDGE,{"derivedFrom":sQuery(id+"F5.wireOp",EDGE,"E320.MirrorCS")}),1.0]])]});
            var Q16;
            Q16=makeQuery(id+"F5.imprint","IMPRINT",FACE,{"disambiguationData":[TD([[makeQuery(id+"F5.imprint","IMPRINT",EDGE,{"derivedFrom":sQuery(id+"F5.wireOp",EDGE,"E304.MirrorCS")}),1.0]])]});
            var Q17;
            Q17=makeQuery(id+"F5.imprint","IMPRINT",FACE,{"disambiguationData":[TD([[makeQuery(id+"F5.imprint","IMPRINT",EDGE,{"derivedFrom":sQuery(id+"F5.wireOp",EDGE,"E482")}),1.0]])]});
            var Q18;
            Q18=makeQuery(id+"F5.imprint","IMPRINT",FACE,{"disambiguationData":[TD([[makeQuery(id+"F5.imprint","IMPRINT",EDGE,{"derivedFrom":sQuery(id+"F5.wireOp",EDGE,"E482")}),-1.0]])]});
            extrude(context, id + "F6", {"entities" : qUnion([Q0, Q1, Q2, Q3, Q4, Q5, Q6, Q7, Q8, Q9, Q10, Q11, Q12, Q13, Q14, Q15, Q16, Q17, Q18]), "endBound" : BoundingType.SYMMETRIC, "depth" : 15 * mm, "offsetDistance" : 25 * mm});
        }
        {
            var Q0;
            Q0=makeQuery(id+"F6.opExtrude","SWEPT_BODY",BODY,{"disambiguationData":[OSD([sQuery(id+"F5.wireOp",EDGE,"E263"),sQuery(id+"F5.wireOp",EDGE,"E264"),sQuery(id+"F5.wireOp",EDGE,"E265"),sQuery(id+"F5.wireOp",EDGE,"E266.MirrorCS"),sQuery(id+"F5.wireOp",EDGE,"E267.MirrorCS"),sQuery(id+"F5.wireOp",EDGE,"E268.MirrorCS")])]});
            var Q1;
            Q1=makeQuery(id+"F6.opExtrude","SWEPT_BODY",BODY,{"disambiguationData":[OSD([sQuery(id+"F5.wireOp",EDGE,"E245"),sQuery(id+"F5.wireOp",EDGE,"E246"),sQuery(id+"F5.wireOp",EDGE,"E247"),sQuery(id+"F5.wireOp",EDGE,"E248.MirrorCS"),sQuery(id+"F5.wireOp",EDGE,"E249.MirrorCS"),sQuery(id+"F5.wireOp",EDGE,"E250.MirrorCS")])]});
            var Q2;
            Q2=makeQuery(id+"F6.opExtrude","SWEPT_BODY",BODY,{"disambiguationData":[OSD([sQuery(id+"F5.wireOp",EDGE,"E272.MirrorCS"),sQuery(id+"F5.wireOp",EDGE,"E273.MirrorCS"),sQuery(id+"F5.wireOp",EDGE,"E274.MirrorCS"),sQuery(id+"F5.wireOp",EDGE,"E275.MirrorCS"),sQuery(id+"F5.wireOp",EDGE,"E276.MirrorCS"),sQuery(id+"F5.wireOp",EDGE,"E277.MirrorCS")])]});
            var Q3;
            Q3=makeQuery(id+"F6.opExtrude","SWEPT_BODY",BODY,{"disambiguationData":[OSD([sQuery(id+"F5.wireOp",EDGE,"E258"),sQuery(id+"F5.wireOp",EDGE,"E259"),sQuery(id+"F5.wireOp",EDGE,"E260.MirrorCS"),sQuery(id+"F5.wireOp",EDGE,"E261.MirrorCS"),sQuery(id+"F5.wireOp",EDGE,"E298.MirrorCS"),sQuery(id+"F5.wireOp",EDGE,"E299.MirrorCS"),sQuery(id+"F5.wireOp",EDGE,"E300.MirrorCS"),sQuery(id+"F5.wireOp",EDGE,"E301.MirrorCS")])]});
            var Q4;
            Q4=makeQuery(id+"F6.opExtrude","SWEPT_BODY",BODY,{"disambiguationData":[OSD([sQuery(id+"F5.wireOp",EDGE,"E279.MirrorCS"),sQuery(id+"F5.wireOp",EDGE,"E280.MirrorCS"),sQuery(id+"F5.wireOp",EDGE,"E281.MirrorCS"),sQuery(id+"F5.wireOp",EDGE,"E282.MirrorCS"),sQuery(id+"F5.wireOp",EDGE,"E283.MirrorCS"),sQuery(id+"F5.wireOp",EDGE,"E284.MirrorCS")])]});
            var Q5;
            Q5=makeQuery(id+"F6.opExtrude","SWEPT_BODY",BODY,{"disambiguationData":[OSD([sQuery(id+"F5.wireOp",EDGE,"E251"),sQuery(id+"F5.wireOp",EDGE,"E252"),sQuery(id+"F5.wireOp",EDGE,"E253"),sQuery(id+"F5.wireOp",EDGE,"E254.MirrorCS"),sQuery(id+"F5.wireOp",EDGE,"E255.MirrorCS"),sQuery(id+"F5.wireOp",EDGE,"E256.MirrorCS")])]});
            var Q6;
            Q6=makeQuery(id+"F6.opExtrude","SWEPT_BODY",BODY,{"disambiguationData":[OSD([sQuery(id+"F5.wireOp",EDGE,"E285.MirrorCS"),sQuery(id+"F5.wireOp",EDGE,"E286.MirrorCS"),sQuery(id+"F5.wireOp",EDGE,"E287.MirrorCS"),sQuery(id+"F5.wireOp",EDGE,"E288.MirrorCS"),sQuery(id+"F5.wireOp",EDGE,"E289.MirrorCS"),sQuery(id+"F5.wireOp",EDGE,"E290.MirrorCS")])]});
            var Q7;
            Q7=makeQuery(id+"F6.opExtrude","SWEPT_BODY",BODY,{"disambiguationData":[OSD([sQuery(id+"F5.wireOp",EDGE,"IZq0Cseo-ozo5-eVDn-hIIC-ZCdG3nIGO29B"),sQuery(id+"F5.wireOp",EDGE,"jD5TgONc-o5aO-Mwn6-jDDA-3cEzYcpxTOwf"),sQuery(id+"F5.wireOp",EDGE,"LfCuJklI-VQkZ-aTAI-zSub-LQBj9R7N5b8l"),sQuery(id+"F5.wireOp",EDGE,"efa70577-9a06-4fb0-91fb-be0cdcfc379a0.MirrorCS"),sQuery(id+"F5.wireOp",EDGE,"10c019dc-1107-4735-93b8-dab4fefa558f0.MirrorCS"),sQuery(id+"F5.wireOp",EDGE,"cea54ea5-59ab-458a-8a44-210833ec76c50.MirrorCS")])]});
            var Q8;
            Q8=makeQuery(id+"F6.opExtrude","SWEPT_BODY",BODY,{"disambiguationData":[OSD([sQuery(id+"F5.wireOp",EDGE,"E292.MirrorCS"),sQuery(id+"F5.wireOp",EDGE,"E293.MirrorCS"),sQuery(id+"F5.wireOp",EDGE,"E294.MirrorCS"),sQuery(id+"F5.wireOp",EDGE,"E295.MirrorCS"),sQuery(id+"F5.wireOp",EDGE,"E296.MirrorCS"),sQuery(id+"F5.wireOp",EDGE,"E297.MirrorCS")])]});
            var Q9;
            Q9=makeQuery(id+"F6.opExtrude","SWEPT_BODY",BODY,{"disambiguationData":[OSD([sQuery(id+"F5.wireOp",EDGE,"E328.MirrorCS"),sQuery(id+"F5.wireOp",EDGE,"E329.MirrorCS"),sQuery(id+"F5.wireOp",EDGE,"E330.MirrorCS"),sQuery(id+"F5.wireOp",EDGE,"E331.MirrorCS"),sQuery(id+"F5.wireOp",EDGE,"E332.MirrorCS"),sQuery(id+"F5.wireOp",EDGE,"E333.MirrorCS")])]});
            var Q10;
            Q10=makeQuery(id+"F6.opExtrude","SWEPT_BODY",BODY,{"disambiguationData":[OSD([sQuery(id+"F5.wireOp",EDGE,"E320.MirrorCS"),sQuery(id+"F5.wireOp",EDGE,"E321.MirrorCS"),sQuery(id+"F5.wireOp",EDGE,"E322.MirrorCS"),sQuery(id+"F5.wireOp",EDGE,"E323.MirrorCS"),sQuery(id+"F5.wireOp",EDGE,"E326.MirrorCS"),sQuery(id+"F5.wireOp",EDGE,"E327.MirrorCS")])]});
            var Q11;
            Q11=makeQuery(id+"F6.opExtrude","SWEPT_BODY",BODY,{"disambiguationData":[OSD([sQuery(id+"F5.wireOp",EDGE,"E316.MirrorCS"),sQuery(id+"F5.wireOp",EDGE,"E317.MirrorCS"),sQuery(id+"F5.wireOp",EDGE,"E318.MirrorCS"),sQuery(id+"F5.wireOp",EDGE,"E319.MirrorCS"),sQuery(id+"F5.wireOp",EDGE,"E324.MirrorCS"),sQuery(id+"F5.wireOp",EDGE,"E325.MirrorCS")])]});
            var Q12;
            Q12=makeQuery(id+"F6.opExtrude","SWEPT_BODY",BODY,{"disambiguationData":[OSD([sQuery(id+"F5.wireOp",EDGE,"E334.MirrorCS"),sQuery(id+"F5.wireOp",EDGE,"E335.MirrorCS"),sQuery(id+"F5.wireOp",EDGE,"E336.MirrorCS"),sQuery(id+"F5.wireOp",EDGE,"E337.MirrorCS"),sQuery(id+"F5.wireOp",EDGE,"E338.MirrorCS"),sQuery(id+"F5.wireOp",EDGE,"E339.MirrorCS")])]});
            var Q13;
            Q13=makeQuery(id+"F6.opExtrude","SWEPT_BODY",BODY,{"disambiguationData":[OSD([sQuery(id+"F5.wireOp",EDGE,"E340.MirrorCS"),sQuery(id+"F5.wireOp",EDGE,"E341.MirrorCS"),sQuery(id+"F5.wireOp",EDGE,"E342.MirrorCS"),sQuery(id+"F5.wireOp",EDGE,"E343.MirrorCS"),sQuery(id+"F5.wireOp",EDGE,"E344.MirrorCS"),sQuery(id+"F5.wireOp",EDGE,"E345.MirrorCS")])]});
            var Q14;
            Q14=makeQuery(id+"F6.opExtrude","SWEPT_BODY",BODY,{"disambiguationData":[OSD([sQuery(id+"F5.wireOp",EDGE,"E308.MirrorCS"),sQuery(id+"F5.wireOp",EDGE,"E309.MirrorCS"),sQuery(id+"F5.wireOp",EDGE,"E310.MirrorCS"),sQuery(id+"F5.wireOp",EDGE,"E311.MirrorCS"),sQuery(id+"F5.wireOp",EDGE,"E314.MirrorCS"),sQuery(id+"F5.wireOp",EDGE,"E315.MirrorCS")])]});
            var Q15;
            Q15=makeQuery(id+"F6.opExtrude","SWEPT_BODY",BODY,{"disambiguationData":[OSD([sQuery(id+"F5.wireOp",EDGE,"E304.MirrorCS"),sQuery(id+"F5.wireOp",EDGE,"E305.MirrorCS"),sQuery(id+"F5.wireOp",EDGE,"E306.MirrorCS"),sQuery(id+"F5.wireOp",EDGE,"E307.MirrorCS"),sQuery(id+"F5.wireOp",EDGE,"E312.MirrorCS"),sQuery(id+"F5.wireOp",EDGE,"E313.MirrorCS")])]});
            var Q16;
            Q16=makeQuery(id+"F6.opExtrude","SWEPT_BODY",BODY,{"disambiguationData":[OSD([sQuery(id+"F5.wireOp",EDGE,"E483"),sQuery(id+"F5.wireOp",EDGE,"E484"),sQuery(id+"F5.wireOp",EDGE,"E485.MirrorCS"),sQuery(id+"F5.wireOp",EDGE,"E486.MirrorCS"),sQuery(id+"F5.wireOp",EDGE,"E488.MirrorCS"),sQuery(id+"F5.wireOp",EDGE,"E489.MirrorCS"),sQuery(id+"F5.wireOp",EDGE,"E490.MirrorCS"),sQuery(id+"F5.wireOp",EDGE,"E491.MirrorCS")])]});
            var Q17;
            Q17=qCreatedBy(makeId("Front.planeOp"),FACE);
            mirror(context, id + "F7", {"entities" : qUnion([Q0, Q1, Q2, Q3, Q4, Q5, Q6, Q7, Q8, Q9, Q10, Q11, Q12, Q13, Q14, Q15, Q16]), "mirrorPlane" : qUnion([Q17])});
        }
        {
            var Q0;
            Q0=makeQuery(id+"F7.opPattern","COPY",BODY,{"derivedFrom":makeQuery(id+"F6.opExtrude","SWEPT_BODY",BODY,{"disambiguationData":[OSD([sQuery(id+"F5.wireOp",EDGE,"E245"),sQuery(id+"F5.wireOp",EDGE,"E246"),sQuery(id+"F5.wireOp",EDGE,"E247"),sQuery(id+"F5.wireOp",EDGE,"E248.MirrorCS"),sQuery(id+"F5.wireOp",EDGE,"E249.MirrorCS"),sQuery(id+"F5.wireOp",EDGE,"E250.MirrorCS")])]}),"instanceName":"1"});
            var Q1;
            Q1=makeQuery(id+"F7.opPattern","COPY",BODY,{"derivedFrom":makeQuery(id+"F6.opExtrude","SWEPT_BODY",BODY,{"disambiguationData":[OSD([sQuery(id+"F5.wireOp",EDGE,"E483"),sQuery(id+"F5.wireOp",EDGE,"E484"),sQuery(id+"F5.wireOp",EDGE,"E485.MirrorCS"),sQuery(id+"F5.wireOp",EDGE,"E486.MirrorCS"),sQuery(id+"F5.wireOp",EDGE,"E488.MirrorCS"),sQuery(id+"F5.wireOp",EDGE,"E489.MirrorCS"),sQuery(id+"F5.wireOp",EDGE,"E490.MirrorCS"),sQuery(id+"F5.wireOp",EDGE,"E491.MirrorCS")])]}),"instanceName":"1"});
            var Q2;
            Q2=makeQuery(id+"F7.opPattern","COPY",BODY,{"derivedFrom":makeQuery(id+"F6.opExtrude","SWEPT_BODY",BODY,{"disambiguationData":[OSD([sQuery(id+"F5.wireOp",EDGE,"E340.MirrorCS"),sQuery(id+"F5.wireOp",EDGE,"E341.MirrorCS"),sQuery(id+"F5.wireOp",EDGE,"E342.MirrorCS"),sQuery(id+"F5.wireOp",EDGE,"E343.MirrorCS"),sQuery(id+"F5.wireOp",EDGE,"E344.MirrorCS"),sQuery(id+"F5.wireOp",EDGE,"E345.MirrorCS")])]}),"instanceName":"1"});
            var Q3;
            Q3=makeQuery(id+"F7.opPattern","COPY",BODY,{"derivedFrom":makeQuery(id+"F6.opExtrude","SWEPT_BODY",BODY,{"disambiguationData":[OSD([sQuery(id+"F5.wireOp",EDGE,"E334.MirrorCS"),sQuery(id+"F5.wireOp",EDGE,"E335.MirrorCS"),sQuery(id+"F5.wireOp",EDGE,"E336.MirrorCS"),sQuery(id+"F5.wireOp",EDGE,"E337.MirrorCS"),sQuery(id+"F5.wireOp",EDGE,"E338.MirrorCS"),sQuery(id+"F5.wireOp",EDGE,"E339.MirrorCS")])]}),"instanceName":"1"});
            var Q4;
            Q4=makeQuery(id+"F7.opPattern","COPY",BODY,{"derivedFrom":makeQuery(id+"F6.opExtrude","SWEPT_BODY",BODY,{"disambiguationData":[OSD([sQuery(id+"F5.wireOp",EDGE,"E328.MirrorCS"),sQuery(id+"F5.wireOp",EDGE,"E329.MirrorCS"),sQuery(id+"F5.wireOp",EDGE,"E330.MirrorCS"),sQuery(id+"F5.wireOp",EDGE,"E331.MirrorCS"),sQuery(id+"F5.wireOp",EDGE,"E332.MirrorCS"),sQuery(id+"F5.wireOp",EDGE,"E333.MirrorCS")])]}),"instanceName":"1"});
            var Q5;
            Q5=makeQuery(id+"F7.opPattern","COPY",BODY,{"derivedFrom":makeQuery(id+"F6.opExtrude","SWEPT_BODY",BODY,{"disambiguationData":[OSD([sQuery(id+"F5.wireOp",EDGE,"E320.MirrorCS"),sQuery(id+"F5.wireOp",EDGE,"E321.MirrorCS"),sQuery(id+"F5.wireOp",EDGE,"E322.MirrorCS"),sQuery(id+"F5.wireOp",EDGE,"E323.MirrorCS"),sQuery(id+"F5.wireOp",EDGE,"E326.MirrorCS"),sQuery(id+"F5.wireOp",EDGE,"E327.MirrorCS")])]}),"instanceName":"1"});
            var Q6;
            Q6=makeQuery(id+"F7.opPattern","COPY",BODY,{"derivedFrom":makeQuery(id+"F6.opExtrude","SWEPT_BODY",BODY,{"disambiguationData":[OSD([sQuery(id+"F5.wireOp",EDGE,"E316.MirrorCS"),sQuery(id+"F5.wireOp",EDGE,"E317.MirrorCS"),sQuery(id+"F5.wireOp",EDGE,"E318.MirrorCS"),sQuery(id+"F5.wireOp",EDGE,"E319.MirrorCS"),sQuery(id+"F5.wireOp",EDGE,"E324.MirrorCS"),sQuery(id+"F5.wireOp",EDGE,"E325.MirrorCS")])]}),"instanceName":"1"});
            var Q7;
            Q7=makeQuery(id+"F7.opPattern","COPY",BODY,{"derivedFrom":makeQuery(id+"F6.opExtrude","SWEPT_BODY",BODY,{"disambiguationData":[OSD([sQuery(id+"F5.wireOp",EDGE,"E308.MirrorCS"),sQuery(id+"F5.wireOp",EDGE,"E309.MirrorCS"),sQuery(id+"F5.wireOp",EDGE,"E310.MirrorCS"),sQuery(id+"F5.wireOp",EDGE,"E311.MirrorCS"),sQuery(id+"F5.wireOp",EDGE,"E314.MirrorCS"),sQuery(id+"F5.wireOp",EDGE,"E315.MirrorCS")])]}),"instanceName":"1"});
            var Q8;
            Q8=makeQuery(id+"F7.opPattern","COPY",BODY,{"derivedFrom":makeQuery(id+"F6.opExtrude","SWEPT_BODY",BODY,{"disambiguationData":[OSD([sQuery(id+"F5.wireOp",EDGE,"E304.MirrorCS"),sQuery(id+"F5.wireOp",EDGE,"E305.MirrorCS"),sQuery(id+"F5.wireOp",EDGE,"E306.MirrorCS"),sQuery(id+"F5.wireOp",EDGE,"E307.MirrorCS"),sQuery(id+"F5.wireOp",EDGE,"E312.MirrorCS"),sQuery(id+"F5.wireOp",EDGE,"E313.MirrorCS")])]}),"instanceName":"1"});
            var Q9;
            Q9=makeQuery(id+"F7.opPattern","COPY",BODY,{"derivedFrom":makeQuery(id+"F6.opExtrude","SWEPT_BODY",BODY,{"disambiguationData":[OSD([sQuery(id+"F5.wireOp",EDGE,"E292.MirrorCS"),sQuery(id+"F5.wireOp",EDGE,"E293.MirrorCS"),sQuery(id+"F5.wireOp",EDGE,"E294.MirrorCS"),sQuery(id+"F5.wireOp",EDGE,"E295.MirrorCS"),sQuery(id+"F5.wireOp",EDGE,"E296.MirrorCS"),sQuery(id+"F5.wireOp",EDGE,"E297.MirrorCS")])]}),"instanceName":"1"});
            var Q10;
            Q10=makeQuery(id+"F7.opPattern","COPY",BODY,{"derivedFrom":makeQuery(id+"F6.opExtrude","SWEPT_BODY",BODY,{"disambiguationData":[OSD([sQuery(id+"F5.wireOp",EDGE,"E285.MirrorCS"),sQuery(id+"F5.wireOp",EDGE,"E286.MirrorCS"),sQuery(id+"F5.wireOp",EDGE,"E287.MirrorCS"),sQuery(id+"F5.wireOp",EDGE,"E288.MirrorCS"),sQuery(id+"F5.wireOp",EDGE,"E289.MirrorCS"),sQuery(id+"F5.wireOp",EDGE,"E290.MirrorCS")])]}),"instanceName":"1"});
            var Q11;
            Q11=makeQuery(id+"F7.opPattern","COPY",BODY,{"derivedFrom":makeQuery(id+"F6.opExtrude","SWEPT_BODY",BODY,{"disambiguationData":[OSD([sQuery(id+"F5.wireOp",EDGE,"E279.MirrorCS"),sQuery(id+"F5.wireOp",EDGE,"E280.MirrorCS"),sQuery(id+"F5.wireOp",EDGE,"E281.MirrorCS"),sQuery(id+"F5.wireOp",EDGE,"E282.MirrorCS"),sQuery(id+"F5.wireOp",EDGE,"E283.MirrorCS"),sQuery(id+"F5.wireOp",EDGE,"E284.MirrorCS")])]}),"instanceName":"1"});
            var Q12;
            Q12=makeQuery(id+"F7.opPattern","COPY",BODY,{"derivedFrom":makeQuery(id+"F6.opExtrude","SWEPT_BODY",BODY,{"disambiguationData":[OSD([sQuery(id+"F5.wireOp",EDGE,"E272.MirrorCS"),sQuery(id+"F5.wireOp",EDGE,"E273.MirrorCS"),sQuery(id+"F5.wireOp",EDGE,"E274.MirrorCS"),sQuery(id+"F5.wireOp",EDGE,"E275.MirrorCS"),sQuery(id+"F5.wireOp",EDGE,"E276.MirrorCS"),sQuery(id+"F5.wireOp",EDGE,"E277.MirrorCS")])]}),"instanceName":"1"});
            var Q13;
            Q13=makeQuery(id+"F7.opPattern","COPY",BODY,{"derivedFrom":makeQuery(id+"F6.opExtrude","SWEPT_BODY",BODY,{"disambiguationData":[OSD([sQuery(id+"F5.wireOp",EDGE,"E263"),sQuery(id+"F5.wireOp",EDGE,"E264"),sQuery(id+"F5.wireOp",EDGE,"E265"),sQuery(id+"F5.wireOp",EDGE,"E266.MirrorCS"),sQuery(id+"F5.wireOp",EDGE,"E267.MirrorCS"),sQuery(id+"F5.wireOp",EDGE,"E268.MirrorCS")])]}),"instanceName":"1"});
            var Q14;
            Q14=makeQuery(id+"F7.opPattern","COPY",BODY,{"derivedFrom":makeQuery(id+"F6.opExtrude","SWEPT_BODY",BODY,{"disambiguationData":[OSD([sQuery(id+"F5.wireOp",EDGE,"E251"),sQuery(id+"F5.wireOp",EDGE,"E252"),sQuery(id+"F5.wireOp",EDGE,"E253"),sQuery(id+"F5.wireOp",EDGE,"E254.MirrorCS"),sQuery(id+"F5.wireOp",EDGE,"E255.MirrorCS"),sQuery(id+"F5.wireOp",EDGE,"E256.MirrorCS")])]}),"instanceName":"1"});
            var Q15;
            Q15=makeQuery(id+"F7.opPattern","COPY",BODY,{"derivedFrom":makeQuery(id+"F6.opExtrude","SWEPT_BODY",BODY,{"disambiguationData":[OSD([sQuery(id+"F5.wireOp",EDGE,"E258"),sQuery(id+"F5.wireOp",EDGE,"E259"),sQuery(id+"F5.wireOp",EDGE,"E260.MirrorCS"),sQuery(id+"F5.wireOp",EDGE,"E261.MirrorCS"),sQuery(id+"F5.wireOp",EDGE,"E298.MirrorCS"),sQuery(id+"F5.wireOp",EDGE,"E299.MirrorCS"),sQuery(id+"F5.wireOp",EDGE,"E300.MirrorCS"),sQuery(id+"F5.wireOp",EDGE,"E301.MirrorCS")])]}),"instanceName":"1"});
            var Q16;
            Q16=makeQuery(id+"F6.opExtrude","SWEPT_BODY",BODY,{"disambiguationData":[OSD([sQuery(id+"F5.wireOp",EDGE,"E251"),sQuery(id+"F5.wireOp",EDGE,"E252"),sQuery(id+"F5.wireOp",EDGE,"E253"),sQuery(id+"F5.wireOp",EDGE,"E254.MirrorCS"),sQuery(id+"F5.wireOp",EDGE,"E255.MirrorCS"),sQuery(id+"F5.wireOp",EDGE,"E256.MirrorCS")])]});
            var Q17;
            Q17=makeQuery(id+"F6.opExtrude","SWEPT_BODY",BODY,{"disambiguationData":[OSD([sQuery(id+"F5.wireOp",EDGE,"E263"),sQuery(id+"F5.wireOp",EDGE,"E264"),sQuery(id+"F5.wireOp",EDGE,"E265"),sQuery(id+"F5.wireOp",EDGE,"E266.MirrorCS"),sQuery(id+"F5.wireOp",EDGE,"E267.MirrorCS"),sQuery(id+"F5.wireOp",EDGE,"E268.MirrorCS")])]});
            var Q18;
            Q18=makeQuery(id+"F6.opExtrude","SWEPT_BODY",BODY,{"disambiguationData":[OSD([sQuery(id+"F5.wireOp",EDGE,"E245"),sQuery(id+"F5.wireOp",EDGE,"E246"),sQuery(id+"F5.wireOp",EDGE,"E247"),sQuery(id+"F5.wireOp",EDGE,"E248.MirrorCS"),sQuery(id+"F5.wireOp",EDGE,"E249.MirrorCS"),sQuery(id+"F5.wireOp",EDGE,"E250.MirrorCS")])]});
            var Q19;
            Q19=makeQuery(id+"F6.opExtrude","SWEPT_BODY",BODY,{"disambiguationData":[OSD([sQuery(id+"F5.wireOp",EDGE,"E258"),sQuery(id+"F5.wireOp",EDGE,"E259"),sQuery(id+"F5.wireOp",EDGE,"E260.MirrorCS"),sQuery(id+"F5.wireOp",EDGE,"E261.MirrorCS"),sQuery(id+"F5.wireOp",EDGE,"E298.MirrorCS"),sQuery(id+"F5.wireOp",EDGE,"E299.MirrorCS"),sQuery(id+"F5.wireOp",EDGE,"E300.MirrorCS"),sQuery(id+"F5.wireOp",EDGE,"E301.MirrorCS")])]});
            var Q20;
            Q20=makeQuery(id+"F6.opExtrude","SWEPT_BODY",BODY,{"disambiguationData":[OSD([sQuery(id+"F5.wireOp",EDGE,"E269"),sQuery(id+"F5.wireOp",EDGE,"E270"),sQuery(id+"F5.wireOp",EDGE,"E302.MirrorCS"),sQuery(id+"F5.wireOp",EDGE,"E303.MirrorCS"),sQuery(id+"F5.wireOp",EDGE,"E364.MirrorCS"),sQuery(id+"F5.wireOp",EDGE,"E396.MirrorCS"),sQuery(id+"F5.wireOp",EDGE,"E470.MirrorCS"),sQuery(id+"F5.wireOp",EDGE,"E475.MirrorCS")])]});
            var Q21;
            Q21=makeQuery(id+"F6.opExtrude","SWEPT_BODY",BODY,{"disambiguationData":[OSD([sQuery(id+"F5.wireOp",EDGE,"E272.MirrorCS"),sQuery(id+"F5.wireOp",EDGE,"E273.MirrorCS"),sQuery(id+"F5.wireOp",EDGE,"E274.MirrorCS"),sQuery(id+"F5.wireOp",EDGE,"E275.MirrorCS"),sQuery(id+"F5.wireOp",EDGE,"E276.MirrorCS"),sQuery(id+"F5.wireOp",EDGE,"E277.MirrorCS")])]});
            var Q22;
            Q22=makeQuery(id+"F6.opExtrude","SWEPT_BODY",BODY,{"disambiguationData":[OSD([sQuery(id+"F5.wireOp",EDGE,"E279.MirrorCS"),sQuery(id+"F5.wireOp",EDGE,"E280.MirrorCS"),sQuery(id+"F5.wireOp",EDGE,"E281.MirrorCS"),sQuery(id+"F5.wireOp",EDGE,"E282.MirrorCS"),sQuery(id+"F5.wireOp",EDGE,"E283.MirrorCS"),sQuery(id+"F5.wireOp",EDGE,"E284.MirrorCS")])]});
            var Q23;
            Q23=makeQuery(id+"F6.opExtrude","SWEPT_BODY",BODY,{"disambiguationData":[OSD([sQuery(id+"F5.wireOp",EDGE,"E285.MirrorCS"),sQuery(id+"F5.wireOp",EDGE,"E286.MirrorCS"),sQuery(id+"F5.wireOp",EDGE,"E287.MirrorCS"),sQuery(id+"F5.wireOp",EDGE,"E288.MirrorCS"),sQuery(id+"F5.wireOp",EDGE,"E289.MirrorCS"),sQuery(id+"F5.wireOp",EDGE,"E290.MirrorCS")])]});
            var Q24;
            Q24=makeQuery(id+"F6.opExtrude","SWEPT_BODY",BODY,{"disambiguationData":[OSD([sQuery(id+"F5.wireOp",EDGE,"E292.MirrorCS"),sQuery(id+"F5.wireOp",EDGE,"E293.MirrorCS"),sQuery(id+"F5.wireOp",EDGE,"E294.MirrorCS"),sQuery(id+"F5.wireOp",EDGE,"E295.MirrorCS"),sQuery(id+"F5.wireOp",EDGE,"E296.MirrorCS"),sQuery(id+"F5.wireOp",EDGE,"E297.MirrorCS")])]});
            var Q25;
            Q25=makeQuery(id+"F6.opExtrude","SWEPT_BODY",BODY,{"disambiguationData":[OSD([sQuery(id+"F5.wireOp",EDGE,"E304.MirrorCS"),sQuery(id+"F5.wireOp",EDGE,"E305.MirrorCS"),sQuery(id+"F5.wireOp",EDGE,"E306.MirrorCS"),sQuery(id+"F5.wireOp",EDGE,"E307.MirrorCS"),sQuery(id+"F5.wireOp",EDGE,"E312.MirrorCS"),sQuery(id+"F5.wireOp",EDGE,"E313.MirrorCS")])]});
            var Q26;
            Q26=makeQuery(id+"F6.opExtrude","SWEPT_BODY",BODY,{"disambiguationData":[OSD([sQuery(id+"F5.wireOp",EDGE,"E308.MirrorCS"),sQuery(id+"F5.wireOp",EDGE,"E309.MirrorCS"),sQuery(id+"F5.wireOp",EDGE,"E310.MirrorCS"),sQuery(id+"F5.wireOp",EDGE,"E311.MirrorCS"),sQuery(id+"F5.wireOp",EDGE,"E314.MirrorCS"),sQuery(id+"F5.wireOp",EDGE,"E315.MirrorCS")])]});
            var Q27;
            Q27=makeQuery(id+"F6.opExtrude","SWEPT_BODY",BODY,{"disambiguationData":[OSD([sQuery(id+"F5.wireOp",EDGE,"E316.MirrorCS"),sQuery(id+"F5.wireOp",EDGE,"E317.MirrorCS"),sQuery(id+"F5.wireOp",EDGE,"E318.MirrorCS"),sQuery(id+"F5.wireOp",EDGE,"E319.MirrorCS"),sQuery(id+"F5.wireOp",EDGE,"E324.MirrorCS"),sQuery(id+"F5.wireOp",EDGE,"E325.MirrorCS")])]});
            var Q28;
            Q28=makeQuery(id+"F6.opExtrude","SWEPT_BODY",BODY,{"disambiguationData":[OSD([sQuery(id+"F5.wireOp",EDGE,"E320.MirrorCS"),sQuery(id+"F5.wireOp",EDGE,"E321.MirrorCS"),sQuery(id+"F5.wireOp",EDGE,"E322.MirrorCS"),sQuery(id+"F5.wireOp",EDGE,"E323.MirrorCS"),sQuery(id+"F5.wireOp",EDGE,"E326.MirrorCS"),sQuery(id+"F5.wireOp",EDGE,"E327.MirrorCS")])]});
            var Q29;
            Q29=makeQuery(id+"F6.opExtrude","SWEPT_BODY",BODY,{"disambiguationData":[OSD([sQuery(id+"F5.wireOp",EDGE,"E328.MirrorCS"),sQuery(id+"F5.wireOp",EDGE,"E329.MirrorCS"),sQuery(id+"F5.wireOp",EDGE,"E330.MirrorCS"),sQuery(id+"F5.wireOp",EDGE,"E331.MirrorCS"),sQuery(id+"F5.wireOp",EDGE,"E332.MirrorCS"),sQuery(id+"F5.wireOp",EDGE,"E333.MirrorCS")])]});
            var Q30;
            Q30=makeQuery(id+"F6.opExtrude","SWEPT_BODY",BODY,{"disambiguationData":[OSD([sQuery(id+"F5.wireOp",EDGE,"E334.MirrorCS"),sQuery(id+"F5.wireOp",EDGE,"E335.MirrorCS"),sQuery(id+"F5.wireOp",EDGE,"E336.MirrorCS"),sQuery(id+"F5.wireOp",EDGE,"E337.MirrorCS"),sQuery(id+"F5.wireOp",EDGE,"E338.MirrorCS"),sQuery(id+"F5.wireOp",EDGE,"E339.MirrorCS")])]});
            var Q31;
            Q31=makeQuery(id+"F6.opExtrude","SWEPT_BODY",BODY,{"disambiguationData":[OSD([sQuery(id+"F5.wireOp",EDGE,"E340.MirrorCS"),sQuery(id+"F5.wireOp",EDGE,"E341.MirrorCS"),sQuery(id+"F5.wireOp",EDGE,"E342.MirrorCS"),sQuery(id+"F5.wireOp",EDGE,"E343.MirrorCS"),sQuery(id+"F5.wireOp",EDGE,"E344.MirrorCS"),sQuery(id+"F5.wireOp",EDGE,"E345.MirrorCS")])]});
            var Q32;
            Q32=makeQuery(id+"F6.opExtrude","SWEPT_BODY",BODY,{"disambiguationData":[OSD([sQuery(id+"F5.wireOp",EDGE,"E483"),sQuery(id+"F5.wireOp",EDGE,"E484"),sQuery(id+"F5.wireOp",EDGE,"E485.MirrorCS"),sQuery(id+"F5.wireOp",EDGE,"E486.MirrorCS"),sQuery(id+"F5.wireOp",EDGE,"E488.MirrorCS"),sQuery(id+"F5.wireOp",EDGE,"E489.MirrorCS"),sQuery(id+"F5.wireOp",EDGE,"E490.MirrorCS"),sQuery(id+"F5.wireOp",EDGE,"E491.MirrorCS")])]});
            var Q33;
            Q33=qCreatedBy(makeId("Top.planeOp"),FACE);
            mirror(context, id + "F8", {"entities" : qUnion([Q0, Q1, Q2, Q3, Q4, Q5, Q6, Q7, Q8, Q9, Q10, Q11, Q12, Q13, Q14, Q15, Q16, Q17, Q18, Q19, Q20, Q21, Q22, Q23, Q24, Q25, Q26, Q27, Q28, Q29, Q30, Q31, Q32]), "mirrorPlane" : qUnion([Q33])});
        }
    });
